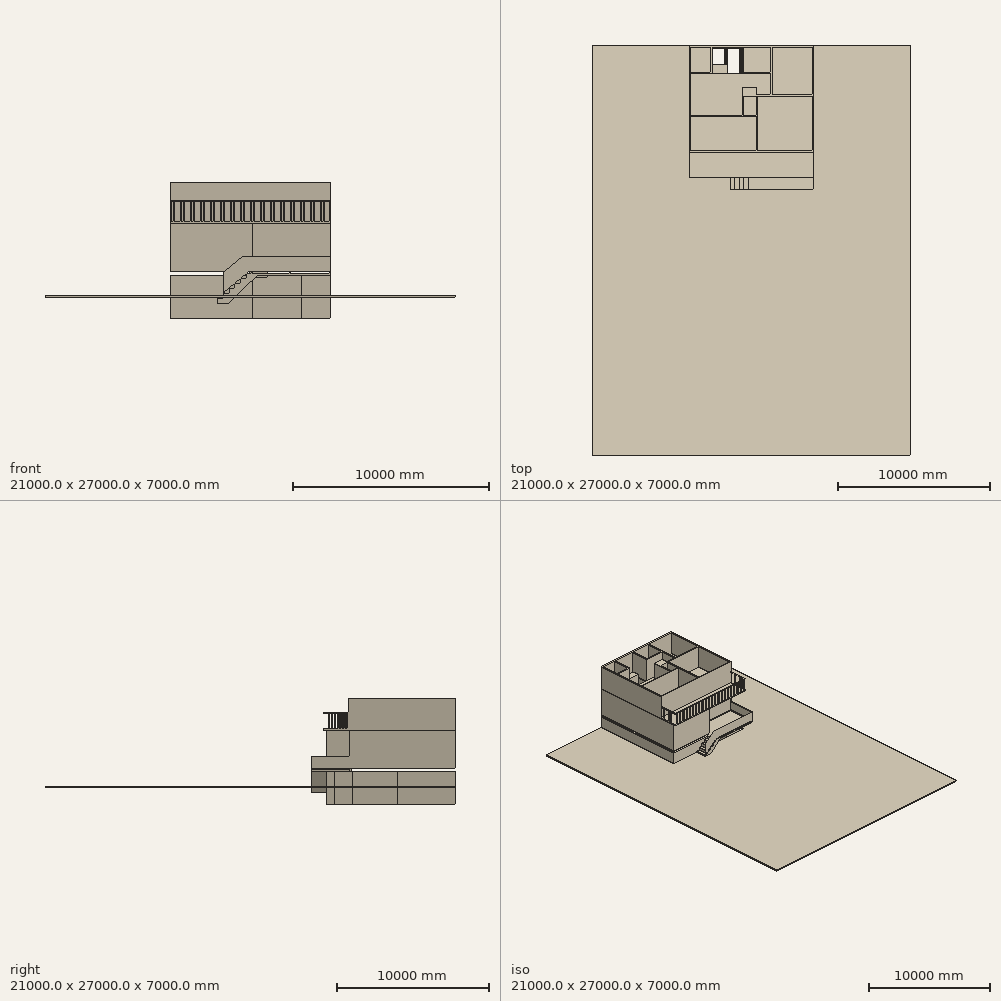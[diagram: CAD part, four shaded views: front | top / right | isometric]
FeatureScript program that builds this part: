
annotation { "Feature Type Name" : "Feature", "Feature Type Description" : "" }
export const myFeature = defineFeature(function(context is Context, id is Id, definition is map)
    precondition{}
    {
        {
            var Q0;
            Q0=qCreatedBy(makeId("Top.planeOp"),FACE);
            var sketch = newSketch(context, id + "F0", { "sketchPlane" : qUnion([Q0])});
            skLineSegment(sketch, "E0", {"start": v(-4100, -4250) * mm, "end": v(-4100, 4250) * mm});
            skLineSegment(sketch, "E1", {"start": v(-4100, 4250) * mm, "end": v(4100, 4250) * mm});
            skLineSegment(sketch, "E2", {"start": v(4100, 4250) * mm, "end": v(4100, -2750) * mm});
            skLineSegment(sketch, "E3", {"start": v(4100, -2750) * mm, "end": v(100, -2750) * mm});
            skLineSegment(sketch, "E4", {"start": v(100, -2750) * mm, "end": v(100, -4250) * mm});
            skLineSegment(sketch, "E5", {"start": v(100, -4250) * mm, "end": v(-4100, -4250) * mm});
            skLineSegment(sketch, "E6", {"start": v(-3950, -4100) * mm, "end": v(-3950, 4100) * mm});
            skLineSegment(sketch, "E7", {"start": v(-3950, 4100) * mm, "end": v(3900, 4100) * mm});
            skLineSegment(sketch, "E8", {"start": v(3900, 4100) * mm, "end": v(3900, -2600) * mm});
            skLineSegment(sketch, "E9", {"start": v(3900, -2600) * mm, "end": v(-50, -2600) * mm});
            skLineSegment(sketch, "E10", {"start": v(-50, -2600) * mm, "end": v(-50, -4100) * mm});
            skLineSegment(sketch, "E11", {"start": v(-50, -4100) * mm, "end": v(-3950, -4100) * mm});
            skLineSegment(sketch, "E12.bottom", {"start": v(-2750, 4100) * mm, "end": v(-2650, 4100) * mm});
            skLineSegment(sketch, "E12.top", {"start": v(-2750, 2100) * mm, "end": v(-2650, 2100) * mm});
            skLineSegment(sketch, "E12.left", {"start": v(-2750, 4100) * mm, "end": v(-2750, 2100) * mm});
            skLineSegment(sketch, "E12.right", {"start": v(-2650, 4100) * mm, "end": v(-2650, 2100) * mm});
            skLineSegment(sketch, "E13", {"start": v(-3950, 3300) * mm, "end": v(-2750, 3300) * mm});
            skLineSegment(sketch, "E14", {"start": v(-3950, 3200) * mm, "end": v(-2750, 3200) * mm});
            skLineSegment(sketch, "E15", {"start": v(-3950, 800) * mm, "end": v(-650, 800) * mm});
            skLineSegment(sketch, "E16", {"start": v(-650, 800) * mm, "end": v(-650, 2100) * mm});
            skLineSegment(sketch, "E17", {"start": v(-650, 2100) * mm, "end": v(-1650, 2100) * mm});
            skLineSegment(sketch, "E18", {"start": v(-1650, 2100) * mm, "end": v(-1650, 4100) * mm});
            skLineSegment(sketch, "E19", {"start": v(-1650, 4100) * mm, "end": v(-1550, 4100) * mm});
            skLineSegment(sketch, "E20", {"start": v(-1550, 4100) * mm, "end": v(-1550, 2200) * mm});
            skLineSegment(sketch, "E21", {"start": v(-1550, 2200) * mm, "end": v(-550, 2200) * mm});
            skLineSegment(sketch, "E22", {"start": v(-550, 2200) * mm, "end": v(-550, 700) * mm});
            skLineSegment(sketch, "E23", {"start": v(-550, 700) * mm, "end": v(-3950, 700) * mm});
            skLineSegment(sketch, "E24", {"start": v(-3950, 700) * mm, "end": v(-3950, 800) * mm});
            skLineSegment(sketch, "E25", {"start": v(-550, 2200) * mm, "end": v(-550, 4100) * mm});
            skLineSegment(sketch, "E26", {"start": v(-650, 4100) * mm, "end": v(-650, 2200) * mm});
            skLineSegment(sketch, "E27", {"start": v(-550, 700) * mm, "end": v(3900, 700) * mm});
            skLineSegment(sketch, "E28", {"start": v(3900, 800) * mm, "end": v(-550, 800) * mm});
            skLineSegment(sketch, "E29", {"start": v(-650, 700) * mm, "end": v(-650, 400) * mm});
            skLineSegment(sketch, "E30", {"start": v(-650, 400) * mm, "end": v(0, -200) * mm});
            skLineSegment(sketch, "E31", {"start": v(0, -200) * mm, "end": v(300, -200) * mm});
            skLineSegment(sketch, "E32", {"start": v(300, -200) * mm, "end": v(300, 0) * mm});
            skLineSegment(sketch, "E33", {"start": v(1800, 4100) * mm, "end": v(1800, 800) * mm});
            skLineSegment(sketch, "E34", {"start": v(1900, 4100) * mm, "end": v(1900, 800) * mm});
            skLineSegment(sketch, "E35", {"start": v(300, 0) * mm, "end": v(300, 1300) * mm});
            skLineSegment(sketch, "E36", {"start": v(300, 1300) * mm, "end": v(-550, 1300) * mm});
            skSolve(sketch);
        }
        {
            var Q0;
            Q0=makeQuery(id+"F0.imprint","IMPRINT",FACE,{"disambiguationData":[TD([[makeQuery(id+"F0.imprint","IMPRINT",EDGE,{"derivedFrom":sQuery(id+"F0.wireOp",EDGE,"E15")}),-1.0]])]});
            var Q1;
            {var subQ3=sQuery(id+"F0.wireOp",EDGE,"E36");Q1=makeQuery(id+"F0.imprint","IMPRINT",FACE,{"disambiguationData":[TD([[makeQuery(id+"F0.imprint","IMPRINT",EDGE,{"derivedFrom":subQ3}),1.0]])]});}
            var Q2;
            {var subQ1=sQuery(id+"F0.wireOp",EDGE,"E22");var subQ3=sQuery(id+"F0.wireOp",EDGE,"E28");var subQ4=makeQuery(id+"F0.imprint","INTERSECT",VERTEX,{"derivedFrom":[subQ1,subQ3]});Q2=makeQuery(id+"F0.imprint","IMPRINT",FACE,{"disambiguationData":[TD([[makeQuery(id+"F0.imprint","IMPRINT",EDGE,{"disambiguationData":[TD([[subQ4,1.0]])],"derivedFrom":subQ3}),1.0]])]});}
            var Q3;
            {var subQ0=sQuery(id+"F0.wireOp",EDGE,"E29");Q3=makeQuery(id+"F0.imprint","IMPRINT",FACE,{"disambiguationData":[TD([[makeQuery(id+"F0.imprint","IMPRINT",EDGE,{"derivedFrom":subQ0}),1.0]])]});}
            var Q4;
            {var subQ3=sQuery(id+"F0.wireOp",EDGE,"E8");var subQ6=sQuery(id+"F0.wireOp",EDGE,"E27");var subQ9=makeQuery(id+"F0.imprint","INTERSECT",VERTEX,{"derivedFrom":[subQ3,subQ6]});Q4=makeQuery(id+"F0.imprint","IMPRINT",FACE,{"disambiguationData":[TD([[makeQuery(id+"F0.imprint","IMPRINT",EDGE,{"disambiguationData":[TD([[subQ9,1.0]])],"derivedFrom":subQ3}),-1.0]])]});}
            var Q5;
            {var subQ0=sQuery(id+"F0.wireOp",EDGE,"E33");Q5=makeQuery(id+"F0.imprint","IMPRINT",FACE,{"disambiguationData":[TD([[makeQuery(id+"F0.imprint","IMPRINT",EDGE,{"derivedFrom":subQ0}),1.0]])]});}
            var Q6;
            Q6=makeQuery(id+"F0.imprint","IMPRINT",FACE,{"disambiguationData":[TD([[makeQuery(id+"F0.imprint","IMPRINT",EDGE,{"derivedFrom":sQuery(id+"F0.wireOp",EDGE,"E0")}),-1.0]])]});
            var Q7;
            {var subQ0=sQuery(id+"F0.wireOp",EDGE,"E13");Q7=makeQuery(id+"F0.imprint","IMPRINT",FACE,{"disambiguationData":[TD([[makeQuery(id+"F0.imprint","IMPRINT",EDGE,{"derivedFrom":subQ0}),-1.0]])]});}
            var Q8;
            {var subQ3=sQuery(id+"F0.wireOp",EDGE,"E12.bottom");Q8=makeQuery(id+"F0.imprint","IMPRINT",FACE,{"disambiguationData":[TD([[makeQuery(id+"F0.imprint","IMPRINT",EDGE,{"derivedFrom":subQ3}),-1.0]])]});}
            var Q9;
            {var subQ0=sQuery(id+"F0.wireOp",EDGE,"E25");Q9=makeQuery(id+"F0.imprint","IMPRINT",FACE,{"disambiguationData":[TD([[makeQuery(id+"F0.imprint","IMPRINT",EDGE,{"derivedFrom":subQ0}),1.0]])]});}
            extrude(context, id + "F1", {"entities" : qUnion([Q0, Q1, Q2, Q3, Q4, Q5, Q6, Q7, Q8, Q9]), "depth" : 2500 * mm, "offsetDistance" : 25 * mm});
        }
        {
            var Q0;
            Q0=makeQuery(id+"F1.opExtrude","CAP_FACE",FACE,{"disambiguationData":[OSD([sQuery(id+"F0.wireOp",EDGE,"E0"),sQuery(id+"F0.wireOp",EDGE,"E1"),sQuery(id+"F0.wireOp",EDGE,"E2"),sQuery(id+"F0.wireOp",EDGE,"E3"),sQuery(id+"F0.wireOp",EDGE,"E4"),sQuery(id+"F0.wireOp",EDGE,"E5"),sQuery(id+"F0.wireOp",EDGE,"E6"),sQuery(id+"F0.wireOp",EDGE,"E7"),sQuery(id+"F0.wireOp",EDGE,"E8"),sQuery(id+"F0.wireOp",EDGE,"E9"),sQuery(id+"F0.wireOp",EDGE,"E10"),sQuery(id+"F0.wireOp",EDGE,"E11"),sQuery(id+"F0.wireOp",EDGE,"E12.top"),sQuery(id+"F0.wireOp",EDGE,"E12.left"),sQuery(id+"F0.wireOp",EDGE,"E12.right"),sQuery(id+"F0.wireOp",EDGE,"E13"),sQuery(id+"F0.wireOp",EDGE,"E14"),sQuery(id+"F0.wireOp",EDGE,"E15"),sQuery(id+"F0.wireOp",EDGE,"E16"),sQuery(id+"F0.wireOp",EDGE,"E17"),sQuery(id+"F0.wireOp",EDGE,"E18"),sQuery(id+"F0.wireOp",EDGE,"E20"),sQuery(id+"F0.wireOp",EDGE,"E21"),sQuery(id+"F0.wireOp",EDGE,"E22"),sQuery(id+"F0.wireOp",EDGE,"E23"),sQuery(id+"F0.wireOp",EDGE,"E25"),sQuery(id+"F0.wireOp",EDGE,"E26"),sQuery(id+"F0.wireOp",EDGE,"E27"),sQuery(id+"F0.wireOp",EDGE,"E28"),sQuery(id+"F0.wireOp",EDGE,"E29"),sQuery(id+"F0.wireOp",EDGE,"E30"),sQuery(id+"F0.wireOp",EDGE,"E31"),sQuery(id+"F0.wireOp",EDGE,"E32")])],"isStart":true});
            cPlane(context, id + "F2", {"entities" : qUnion([Q0]), "cplaneType" : CPlaneType.OFFSET, "offset" : 200 * mm, "width" : 150 * mm, "height" : 150 * mm});
        }
        {
            var Q0;
            Q0=makeQuery(id+"F1.opExtrude","SWEPT_FACE",FACE,{"disambiguationData":[OSD([sQuery(id+"F0.wireOp",EDGE,"E9")])]});
            var sketch = newSketch(context, id + "F3", { "sketchPlane" : qUnion([Q0])});
            skLineSegment(sketch, "E37.bottom", {"start": v(50, 1) * mm, "end": v(-850, 1) * mm});
            skLineSegment(sketch, "E37.top", {"start": v(50, -299) * mm, "end": v(-850, -299) * mm});
            skLineSegment(sketch, "E37.left", {"start": v(50, 1) * mm, "end": v(50, -299) * mm});
            skLineSegment(sketch, "E37.right", {"start": v(-850, 1) * mm, "end": v(-850, -299) * mm});
            skSolve(sketch);
        }
        {
            var Q0;
            Q0=qCreatedBy(id+"F2.planeOp",FACE);
            var sketch = newSketch(context, id + "F4", { "sketchPlane" : qUnion([Q0])});
            skLineSegment(sketch, "E38.bottom", {"start": v(100, 2750) * mm, "end": v(4100, 2750) * mm});
            skLineSegment(sketch, "E38.top", {"start": v(100, 5250) * mm, "end": v(4100, 5250) * mm});
            skLineSegment(sketch, "E38.left", {"start": v(100, 2750) * mm, "end": v(100, 5250) * mm});
            skLineSegment(sketch, "E38.right", {"start": v(4100, 2750) * mm, "end": v(4100, 5250) * mm});
            skSolve(sketch);
        }
        {
            var Q0;
            {var subQ0=sQuery(id+"F3.wireOp",EDGE,"E37.top");Q0=makeQuery(id+"F3.imprint","IMPRINT",FACE,{"disambiguationData":[TD([[makeQuery(id+"F3.imprint","IMPRINT",EDGE,{"derivedFrom":subQ0}),-1.0]])]});}
            extrude(context, id + "F5", {"entities" : qUnion([Q0]), "operationType" : NewBodyOperationType.ADD, "oppositeDirection" : true, "depth" : 400 * mm, "offsetDistance" : 25 * mm});
        }
        {
            var Q0;
            Q0=makeQuery(id+"F4.imprint","IMPRINT",FACE,{"disambiguationData":[TD([[makeQuery(id+"F4.imprint","IMPRINT",EDGE,{"derivedFrom":sQuery(id+"F4.wireOp",EDGE,"E38.bottom")}),1.0]])]});
            extrude(context, id + "F6", {"entities" : qUnion([Q0]), "operationType" : NewBodyOperationType.ADD, "oppositeDirection" : true, "depth" : 100 * mm, "offsetDistance" : 25 * mm});
        }
        {
            var Q0;
            Q0=makeQuery(id+"F6.opExtrude","SWEPT_FACE",FACE,{"disambiguationData":[OSD([sQuery(id+"F4.wireOp",EDGE,"E38.top")])]});
            var sketch = newSketch(context, id + "F7", { "sketchPlane" : qUnion([Q0])});
            skLineSegment(sketch, "E39", {"start": v(100, -100) * mm, "end": v(-200, -100) * mm});
            skLineSegment(sketch, "E40", {"start": v(-200, -100) * mm, "end": v(-200, -350) * mm});
            skLineSegment(sketch, "E41", {"start": v(-200, -350) * mm, "end": v(-500, -350) * mm});
            skLineSegment(sketch, "E42", {"start": v(-500, -350) * mm, "end": v(-500, -600) * mm});
            skLineSegment(sketch, "E43", {"start": v(-500, -600) * mm, "end": v(-800, -600) * mm});
            skLineSegment(sketch, "E44", {"start": v(-800, -600) * mm, "end": v(-800, -850) * mm});
            skLineSegment(sketch, "E45", {"start": v(-800, -850) * mm, "end": v(-1100, -850) * mm});
            skLineSegment(sketch, "E46", {"start": v(-1100, -850) * mm, "end": v(-1100, -1100) * mm});
            skLineSegment(sketch, "E47", {"start": v(-1100, -1100) * mm, "end": v(-1400, -1100) * mm});
            skLineSegment(sketch, "E48", {"start": v(-1400, -1100) * mm, "end": v(-1400, -1350) * mm});
            skLineSegment(sketch, "E49", {"start": v(-1400, -1350) * mm, "end": v(-1700, -1350) * mm});
            skLineSegment(sketch, "E50", {"start": v(-1700, -1350) * mm, "end": v(-1700, -1600) * mm});
            skLineSegment(sketch, "E51", {"start": v(-1700, -1600) * mm, "end": v(-1108.65, -1600) * mm});
            skLineSegment(sketch, "E52", {"start": v(-1108.65, -1600) * mm, "end": v(350, -200) * mm});
            skLineSegment(sketch, "E53", {"start": v(350, -200) * mm, "end": v(100, -100) * mm});
            skSolve(sketch);
        }
        {
            var Q0;
            Q0=makeQuery(id+"F7.imprint","IMPRINT",FACE,{"disambiguationData":[TD([[makeQuery(id+"F7.imprint","IMPRINT",EDGE,{"derivedFrom":sQuery(id+"F7.wireOp",EDGE,"E39")}),1.0]])]});
            var Q1;
            Q1=makeQuery(id+"F1.opExtrude","SWEPT_FACE",FACE,{"disambiguationData":[OSD([sQuery(id+"F0.wireOp",EDGE,"E5")])]});
            extrude(context, id + "F8", {"entities" : qUnion([Q0]), "operationType" : NewBodyOperationType.ADD, "endBound" : BoundingType.UP_TO_SURFACE, "oppositeDirection" : true, "depth" : 25 * mm, "endBoundEntityFace" : qUnion([Q1]), "offsetDistance" : 25 * mm});
        }
        {
            var Q0;
            {var subQ0=sQuery(id+"F4.wireOp",EDGE,"E38.top");Q0=makeQuery(id+"F8.boolean.opBoolean","MERGE",FACE,{"derivedFrom":[makeQuery(id+"F6.opExtrude","SWEPT_FACE",FACE,{"disambiguationData":[OSD([subQ0])]}),makeQuery(id+"F8.opExtrude","CAP_FACE",FACE,{"disambiguationData":[OSD([subQ0,sQuery(id+"F4.wireOp",EDGE,"E38.left"),sQuery(id+"F7.wireOp",EDGE,"E39"),sQuery(id+"F7.wireOp",EDGE,"E40"),sQuery(id+"F7.wireOp",EDGE,"E41"),sQuery(id+"F7.wireOp",EDGE,"E42"),sQuery(id+"F7.wireOp",EDGE,"E43"),sQuery(id+"F7.wireOp",EDGE,"E44"),sQuery(id+"F7.wireOp",EDGE,"E45"),sQuery(id+"F7.wireOp",EDGE,"E46"),sQuery(id+"F7.wireOp",EDGE,"E47"),sQuery(id+"F7.wireOp",EDGE,"E48"),sQuery(id+"F7.wireOp",EDGE,"E49"),sQuery(id+"F7.wireOp",EDGE,"E50"),sQuery(id+"F7.wireOp",EDGE,"E51"),sQuery(id+"F7.wireOp",EDGE,"E52")])],"isStart":true})]});}
            var sketch = newSketch(context, id + "F9", { "sketchPlane" : qUnion([Q0])});
            skLineSegment(sketch, "E54", {"start": v(-1400, -1100) * mm, "end": v(-1400, -45.62) * mm});
            skLineSegment(sketch, "E55", {"start": v(-1400, -45.62) * mm, "end": v(-385.26, 800) * mm});
            skLineSegment(sketch, "E56", {"start": v(-385.26, 800) * mm, "end": v(4100, 800) * mm});
            skLineSegment(sketch, "E57", {"start": v(4100, 800) * mm, "end": v(4100, -100) * mm});
            skLineSegment(sketch, "E58", {"start": v(4100, -100) * mm, "end": v(4050, -100) * mm});
            skLineSegment(sketch, "E59", {"start": v(4050, -100) * mm, "end": v(4050, 0) * mm});
            skLineSegment(sketch, "E60", {"start": v(4050, 0) * mm, "end": v(2070.72, 0) * mm});
            skLineSegment(sketch, "E61", {"start": v(2070.72, 0) * mm, "end": v(2070.72, -100) * mm});
            skLineSegment(sketch, "E62", {"start": v(2070.72, -100) * mm, "end": v(2020.72, -100) * mm});
            skLineSegment(sketch, "E63", {"start": v(2020.72, -100) * mm, "end": v(2020.72, 0) * mm});
            skLineSegment(sketch, "E64", {"start": v(2020.72, 0) * mm, "end": v(100, 0) * mm});
            skLineSegment(sketch, "E65", {"start": v(100, 0) * mm, "end": v(100, -100) * mm});
            skLineSegment(sketch, "E66", {"start": v(100, -100) * mm, "end": v(50, -100) * mm});
            skLineSegment(sketch, "E67", {"start": v(50, -100) * mm, "end": v(50, 0) * mm});
            skLineSegment(sketch, "E68", {"start": v(50, 0) * mm, "end": v(-95.62, 0) * mm});
            skLineSegment(sketch, "E69", {"start": v(-95.62, 0) * mm, "end": v(-1350, -1045.32) * mm});
            skLineSegment(sketch, "E70", {"start": v(-1350, -1045.32) * mm, "end": v(-1350, -1100) * mm});
            skLineSegment(sketch, "E71", {"start": v(-1350, -1100) * mm, "end": v(-1400, -1100) * mm});
            skSolve(sketch);
        }
        {
            var Q0;
            Q0=makeQuery(id+"F9.imprint","IMPRINT",FACE,{"disambiguationData":[TD([[makeQuery(id+"F9.imprint","IMPRINT",EDGE,{"derivedFrom":sQuery(id+"F9.wireOp",EDGE,"E54")}),-1.0]])]});
            extrude(context, id + "F10", {"entities" : qUnion([Q0]), "operationType" : NewBodyOperationType.ADD, "oppositeDirection" : true, "depth" : 10 * mm, "offsetDistance" : 25 * mm});
        }
        {
            var Q0;
            Q0=makeQuery(id+"F10.boolean.opBoolean","MERGE",FACE,{"derivedFrom":[makeQuery(id+"F6.opExtrude","SWEPT_FACE",FACE,{"disambiguationData":[OSD([sQuery(id+"F4.wireOp",EDGE,"E38.right")])]}),makeQuery(id+"F10.opExtrude","SWEPT_FACE",FACE,{"disambiguationData":[OSD([sQuery(id+"F9.wireOp",EDGE,"E57")])]})]});
            var sketch = newSketch(context, id + "F11", { "sketchPlane" : qUnion([Q0])});
            skLineSegment(sketch, "E72.bottom", {"start": v(-5250, 800) * mm, "end": v(-2750, 800) * mm});
            skLineSegment(sketch, "E72.top", {"start": v(-5250, 0) * mm, "end": v(-2750, 0) * mm});
            skLineSegment(sketch, "E72.left", {"start": v(-5250, 800) * mm, "end": v(-5250, 0) * mm});
            skLineSegment(sketch, "E72.right", {"start": v(-2750, 800) * mm, "end": v(-2750, 0) * mm});
            skSolve(sketch);
        }
        {
            var Q0;
            {var subQ3=sQuery(id+"F11.wireOp",EDGE,"E72.right");Q0=makeQuery(id+"F11.imprint","IMPRINT",FACE,{"disambiguationData":[TD([[makeQuery(id+"F11.imprint","IMPRINT",EDGE,{"derivedFrom":subQ3}),-1.0]])]});}
            extrude(context, id + "F12", {"entities" : qUnion([Q0]), "operationType" : NewBodyOperationType.ADD, "oppositeDirection" : true, "depth" : 10 * mm, "offsetDistance" : 25 * mm});
        }
        {
            var Q0;
            Q0=makeQuery(id+"F1.opExtrude","CAP_FACE",FACE,{"disambiguationData":[OSD([sQuery(id+"F0.wireOp",EDGE,"E0"),sQuery(id+"F0.wireOp",EDGE,"E1"),sQuery(id+"F0.wireOp",EDGE,"E2"),sQuery(id+"F0.wireOp",EDGE,"E3"),sQuery(id+"F0.wireOp",EDGE,"E4"),sQuery(id+"F0.wireOp",EDGE,"E5"),sQuery(id+"F0.wireOp",EDGE,"E6"),sQuery(id+"F0.wireOp",EDGE,"E7"),sQuery(id+"F0.wireOp",EDGE,"E8"),sQuery(id+"F0.wireOp",EDGE,"E9"),sQuery(id+"F0.wireOp",EDGE,"E10"),sQuery(id+"F0.wireOp",EDGE,"E11"),sQuery(id+"F0.wireOp",EDGE,"E12.top"),sQuery(id+"F0.wireOp",EDGE,"E12.left"),sQuery(id+"F0.wireOp",EDGE,"E12.right"),sQuery(id+"F0.wireOp",EDGE,"E13"),sQuery(id+"F0.wireOp",EDGE,"E14"),sQuery(id+"F0.wireOp",EDGE,"E15"),sQuery(id+"F0.wireOp",EDGE,"E16"),sQuery(id+"F0.wireOp",EDGE,"E17"),sQuery(id+"F0.wireOp",EDGE,"E18"),sQuery(id+"F0.wireOp",EDGE,"E20"),sQuery(id+"F0.wireOp",EDGE,"E21"),sQuery(id+"F0.wireOp",EDGE,"E22"),sQuery(id+"F0.wireOp",EDGE,"E23"),sQuery(id+"F0.wireOp",EDGE,"E25"),sQuery(id+"F0.wireOp",EDGE,"E26"),sQuery(id+"F0.wireOp",EDGE,"E27"),sQuery(id+"F0.wireOp",EDGE,"E28"),sQuery(id+"F0.wireOp",EDGE,"E29"),sQuery(id+"F0.wireOp",EDGE,"E30"),sQuery(id+"F0.wireOp",EDGE,"E31"),sQuery(id+"F0.wireOp",EDGE,"E32")])],"isStart":false});
            cPlane(context, id + "F13", {"entities" : qUnion([Q0]), "cplaneType" : CPlaneType.OFFSET, "offset" : 0 * mm, "width" : 150 * mm, "height" : 150 * mm});
        }
        {
            var Q0;
            Q0=qCreatedBy(id+"F13.planeOp",FACE);
            var sketch = newSketch(context, id + "F14", { "sketchPlane" : qUnion([Q0])});
            skLineSegment(sketch, "E73.bottom", {"start": v(-4100, 4250) * mm, "end": v(4100, 4250) * mm});
            skLineSegment(sketch, "E73.top", {"start": v(-4100, -4450) * mm, "end": v(4100, -4450) * mm});
            skLineSegment(sketch, "E73.left", {"start": v(-4100, 4250) * mm, "end": v(-4100, -4450) * mm});
            skLineSegment(sketch, "E73.right", {"start": v(4100, 4250) * mm, "end": v(4100, -4450) * mm});
            skLineSegment(sketch, "E74.bottom", {"start": v(-2600, 4100) * mm, "end": v(-600, 4100) * mm});
            skLineSegment(sketch, "E74.top", {"start": v(-2600, 2400) * mm, "end": v(-600, 2400) * mm});
            skLineSegment(sketch, "E74.left", {"start": v(-2600, 4100) * mm, "end": v(-2600, 2400) * mm});
            skLineSegment(sketch, "E74.right", {"start": v(-600, 4100) * mm, "end": v(-600, 2400) * mm});
            skSolve(sketch);
        }
        {
            var Q0;
            Q0=makeQuery(id+"F14.imprint","IMPRINT",FACE,{"disambiguationData":[TD([[makeQuery(id+"F14.imprint","IMPRINT",EDGE,{"derivedFrom":sQuery(id+"F14.wireOp",EDGE,"E73.bottom")}),-1.0]])]});
            extrude(context, id + "F15", {"entities" : qUnion([Q0]), "depth" : 100 * mm, "offsetDistance" : 25 * mm});
        }
        {
            var Q0;
            Q0=makeQuery(id+"F15.opExtrude","CAP_FACE",FACE,{"disambiguationData":[OSD([sQuery(id+"F14.wireOp",EDGE,"E73.bottom"),sQuery(id+"F14.wireOp",EDGE,"E73.top"),sQuery(id+"F14.wireOp",EDGE,"E73.left"),sQuery(id+"F14.wireOp",EDGE,"E73.right")])],"isStart":false});
            var sketch = newSketch(context, id + "F16", { "sketchPlane" : qUnion([Q0])});
            skLineSegment(sketch, "E75", {"start": v(-4100, -2780) * mm, "end": v(4100, -2780) * mm});
            skLineSegment(sketch, "E76", {"start": v(-2600, 4100) * mm, "end": v(-4000, 4100) * mm});
            skLineSegment(sketch, "E77", {"start": v(-4000, 4100) * mm, "end": v(-4000, -2680) * mm});
            skLineSegment(sketch, "E78", {"start": v(-4000, -2680) * mm, "end": v(4000, -2680) * mm});
            skLineSegment(sketch, "E79", {"start": v(4000, -2680) * mm, "end": v(4000, 4100) * mm});
            skLineSegment(sketch, "E80", {"start": v(4000, 4100) * mm, "end": v(-2600, 4100) * mm});
            skLineSegment(sketch, "E81", {"start": v(-2700, 4100) * mm, "end": v(-2700, 2500) * mm});
            skLineSegment(sketch, "E82", {"start": v(-2700, 2500) * mm, "end": v(-4000, 2500) * mm});
            skLineSegment(sketch, "E83", {"start": v(-4000, 2500) * mm, "end": v(-4000, 2400) * mm});
            skLineSegment(sketch, "E84", {"start": v(-4000, 2400) * mm, "end": v(-2600, 2400) * mm});
            skLineSegment(sketch, "E85", {"start": v(-2600, 2400) * mm, "end": v(-2600, 4100) * mm});
            skLineSegment(sketch, "E86", {"start": v(-2600, 4100) * mm, "end": v(-2700, 4100) * mm});
            skLineSegment(sketch, "E87", {"start": v(-600, 4100) * mm, "end": v(-600, 2400) * mm});
            skLineSegment(sketch, "E88", {"start": v(-600, 2400) * mm, "end": v(1350, 2400) * mm});
            skLineSegment(sketch, "E89", {"start": v(1350, 2400) * mm, "end": v(1350, 4100) * mm});
            skLineSegment(sketch, "E90", {"start": v(1350, 4100) * mm, "end": v(-600, 4100) * mm});
            skLineSegment(sketch, "E91", {"start": v(-500, 4100) * mm, "end": v(-500, 2500) * mm});
            skLineSegment(sketch, "E92", {"start": v(-500, 2500) * mm, "end": v(1250, 2500) * mm});
            skLineSegment(sketch, "E93", {"start": v(1250, 2500) * mm, "end": v(1250, 4100) * mm});
            skLineSegment(sketch, "E94", {"start": v(1350, 2400) * mm, "end": v(1350, 1000) * mm});
            skLineSegment(sketch, "E95", {"start": v(1350, 1000) * mm, "end": v(4000, 1000) * mm});
            skLineSegment(sketch, "E96", {"start": v(4000, 1000) * mm, "end": v(4000, 900) * mm});
            skLineSegment(sketch, "E97", {"start": v(4000, 900) * mm, "end": v(1250, 900) * mm});
            skLineSegment(sketch, "E98", {"start": v(1250, 900) * mm, "end": v(1250, 2400) * mm});
            skLineSegment(sketch, "E99", {"start": v(1250, 2400) * mm, "end": v(1350, 2400) * mm});
            skLineSegment(sketch, "E100", {"start": v(1250, 900) * mm, "end": v(-500, 900) * mm});
            skLineSegment(sketch, "E101", {"start": v(-500, 900) * mm, "end": v(-500, -340) * mm});
            skPoint(sketch, "E101.endSnap0", {"position": v(0, -2680) * mm});
            skLineSegment(sketch, "E102", {"start": v(-500, -2680) * mm, "end": v(-600, -2680) * mm});
            skLineSegment(sketch, "E103", {"start": v(-600, -340) * mm, "end": v(-600, 1000) * mm});
            skLineSegment(sketch, "E104", {"start": v(-600, 1000) * mm, "end": v(1250, 1000) * mm});
            skLineSegment(sketch, "E105", {"start": v(1250, 1000) * mm, "end": v(1250, 900) * mm});
            skLineSegment(sketch, "E106", {"start": v(-4000, -340) * mm, "end": v(-600, -340) * mm});
            skLineSegment(sketch, "E107", {"start": v(300, -440) * mm, "end": v(-4000, -440) * mm});
            skLineSegment(sketch, "E108", {"start": v(-4000, -440) * mm, "end": v(-4000, -340) * mm});
            skLineSegment(sketch, "E109", {"start": v(-2600, 2400) * mm, "end": v(-1600, 2400) * mm});
            skLineSegment(sketch, "E110", {"start": v(-4100, -2780) * mm, "end": v(-4100, 4250) * mm});
            skLineSegment(sketch, "E111", {"start": v(-4100, 4250) * mm, "end": v(4100, 4250) * mm});
            skLineSegment(sketch, "E112", {"start": v(4100, 4250) * mm, "end": v(4100, -2780) * mm});
            skLineSegment(sketch, "E113", {"start": v(-1600, 2400) * mm, "end": v(-1600, 3000) * mm});
            skLineSegment(sketch, "E114", {"start": v(-1600, 3000) * mm, "end": v(-2600, 3000) * mm});
            skLineSegment(sketch, "E115", {"start": v(-600, 1000) * mm, "end": v(-600, 1500) * mm});
            skLineSegment(sketch, "E116", {"start": v(-600, 1500) * mm, "end": v(350, 1500) * mm});
            skLineSegment(sketch, "E117", {"start": v(350, 1500) * mm, "end": v(350, 1000) * mm});
            skPoint(sketch, "E118.endSnap0", {"position": v(375, 900) * mm});
            skLineSegment(sketch, "E119", {"start": v(300, -2680) * mm, "end": v(300, 900) * mm});
            skLineSegment(sketch, "E120", {"start": v(400, 900) * mm, "end": v(400, -2680) * mm});
            skLineSegment(sketch, "E121", {"start": v(-500, -340) * mm, "end": v(300, -340) * mm});
            skLineSegment(sketch, "E122.bottom", {"start": v(-4100, -2880) * mm, "end": v(-4070, -2880) * mm});
            skLineSegment(sketch, "E122.top", {"start": v(-4100, -2910) * mm, "end": v(-4070, -2910) * mm});
            skLineSegment(sketch, "E122.left", {"start": v(-4100, -2880) * mm, "end": v(-4100, -2910) * mm});
            skLineSegment(sketch, "E122.right", {"start": v(-4070, -2880) * mm, "end": v(-4070, -2910) * mm});
            skLineSegment(sketch, "E123.0.1.0", {"start": v(-4100, -3080) * mm, "end": v(-4100, -3110) * mm});
            skLineSegment(sketch, "E123.0.1.1", {"start": v(-4100, -3080) * mm, "end": v(-4070, -3080) * mm});
            skLineSegment(sketch, "E123.0.1.2", {"start": v(-4070, -3080) * mm, "end": v(-4070, -3110) * mm});
            skLineSegment(sketch, "E123.0.1.3", {"start": v(-4100, -3110) * mm, "end": v(-4070, -3110) * mm});
            skLineSegment(sketch, "E123.0.2.0", {"start": v(-4100, -3280) * mm, "end": v(-4100, -3310) * mm});
            skLineSegment(sketch, "E123.0.2.1", {"start": v(-4100, -3280) * mm, "end": v(-4070, -3280) * mm});
            skLineSegment(sketch, "E123.0.2.2", {"start": v(-4070, -3280) * mm, "end": v(-4070, -3310) * mm});
            skLineSegment(sketch, "E123.0.2.3", {"start": v(-4100, -3310) * mm, "end": v(-4070, -3310) * mm});
            skLineSegment(sketch, "E123.0.3.0", {"start": v(-4100, -3480) * mm, "end": v(-4100, -3510) * mm});
            skLineSegment(sketch, "E123.0.3.1", {"start": v(-4100, -3480) * mm, "end": v(-4070, -3480) * mm});
            skLineSegment(sketch, "E123.0.3.2", {"start": v(-4070, -3480) * mm, "end": v(-4070, -3510) * mm});
            skLineSegment(sketch, "E123.0.3.3", {"start": v(-4100, -3510) * mm, "end": v(-4070, -3510) * mm});
            skLineSegment(sketch, "E123.0.4.0", {"start": v(-4100, -3680) * mm, "end": v(-4100, -3710) * mm});
            skLineSegment(sketch, "E123.0.4.1", {"start": v(-4100, -3680) * mm, "end": v(-4070, -3680) * mm});
            skLineSegment(sketch, "E123.0.4.2", {"start": v(-4070, -3680) * mm, "end": v(-4070, -3710) * mm});
            skLineSegment(sketch, "E123.0.4.3", {"start": v(-4100, -3710) * mm, "end": v(-4070, -3710) * mm});
            skLineSegment(sketch, "E123.0.5.0", {"start": v(-4100, -3880) * mm, "end": v(-4100, -3910) * mm});
            skLineSegment(sketch, "E123.0.5.1", {"start": v(-4100, -3880) * mm, "end": v(-4070, -3880) * mm});
            skLineSegment(sketch, "E123.0.5.2", {"start": v(-4070, -3880) * mm, "end": v(-4070, -3910) * mm});
            skLineSegment(sketch, "E123.0.5.3", {"start": v(-4100, -3910) * mm, "end": v(-4070, -3910) * mm});
            skLineSegment(sketch, "E123.0.6.0", {"start": v(-4100, -4080) * mm, "end": v(-4100, -4110) * mm});
            skLineSegment(sketch, "E123.0.6.1", {"start": v(-4100, -4080) * mm, "end": v(-4070, -4080) * mm});
            skLineSegment(sketch, "E123.0.6.2", {"start": v(-4070, -4080) * mm, "end": v(-4070, -4110) * mm});
            skLineSegment(sketch, "E123.0.6.3", {"start": v(-4100, -4110) * mm, "end": v(-4070, -4110) * mm});
            skLineSegment(sketch, "E123.0.7.0", {"start": v(-4100, -4280) * mm, "end": v(-4100, -4310) * mm});
            skLineSegment(sketch, "E123.0.7.1", {"start": v(-4100, -4280) * mm, "end": v(-4070, -4280) * mm});
            skLineSegment(sketch, "E123.0.7.2", {"start": v(-4070, -4280) * mm, "end": v(-4070, -4310) * mm});
            skLineSegment(sketch, "E123.0.7.3", {"start": v(-4100, -4310) * mm, "end": v(-4070, -4310) * mm});
            skLineSegment(sketch, "E123.direction1", {"start": v(-4100, -2910) * mm, "end": v(-4075, -2910) * mm, "construction": true});
            skLineSegment(sketch, "E123.direction2", {"start": v(-4100, -2910) * mm, "end": v(-4100, -3110) * mm, "construction": true});
            skLineSegment(sketch, "E124.bottom", {"start": v(-4100, -4450) * mm, "end": v(-4070, -4450) * mm});
            skLineSegment(sketch, "E124.top", {"start": v(-4100, -4420) * mm, "end": v(-4070, -4420) * mm});
            skLineSegment(sketch, "E124.left", {"start": v(-4100, -4450) * mm, "end": v(-4100, -4420) * mm});
            skLineSegment(sketch, "E124.right", {"start": v(-4070, -4450) * mm, "end": v(-4070, -4420) * mm});
            skLineSegment(sketch, "E125.1.0.0", {"start": v(-3929.17, -4420) * mm, "end": v(-3899.17, -4420) * mm});
            skLineSegment(sketch, "E125.1.0.1", {"start": v(-3899.17, -4450) * mm, "end": v(-3899.17, -4420) * mm});
            skLineSegment(sketch, "E125.1.0.2", {"start": v(-3929.17, -4450) * mm, "end": v(-3899.17, -4450) * mm});
            skLineSegment(sketch, "E125.1.0.3", {"start": v(-3929.17, -4450) * mm, "end": v(-3929.17, -4420) * mm});
            skLineSegment(sketch, "E125.2.0.0", {"start": v(-3758.33, -4420) * mm, "end": v(-3728.33, -4420) * mm});
            skLineSegment(sketch, "E125.2.0.1", {"start": v(-3728.33, -4450) * mm, "end": v(-3728.33, -4420) * mm});
            skLineSegment(sketch, "E125.2.0.2", {"start": v(-3758.33, -4450) * mm, "end": v(-3728.33, -4450) * mm});
            skLineSegment(sketch, "E125.2.0.3", {"start": v(-3758.33, -4450) * mm, "end": v(-3758.33, -4420) * mm});
            skLineSegment(sketch, "E125.3.0.0", {"start": v(-3587.5, -4420) * mm, "end": v(-3557.5, -4420) * mm});
            skLineSegment(sketch, "E125.3.0.1", {"start": v(-3557.5, -4450) * mm, "end": v(-3557.5, -4420) * mm});
            skLineSegment(sketch, "E125.3.0.2", {"start": v(-3587.5, -4450) * mm, "end": v(-3557.5, -4450) * mm});
            skLineSegment(sketch, "E125.3.0.3", {"start": v(-3587.5, -4450) * mm, "end": v(-3587.5, -4420) * mm});
            skLineSegment(sketch, "E125.4.0.0", {"start": v(-3416.67, -4420) * mm, "end": v(-3386.67, -4420) * mm});
            skLineSegment(sketch, "E125.4.0.1", {"start": v(-3386.67, -4450) * mm, "end": v(-3386.67, -4420) * mm});
            skLineSegment(sketch, "E125.4.0.2", {"start": v(-3416.67, -4450) * mm, "end": v(-3386.67, -4450) * mm});
            skLineSegment(sketch, "E125.4.0.3", {"start": v(-3416.67, -4450) * mm, "end": v(-3416.67, -4420) * mm});
            skLineSegment(sketch, "E125.5.0.0", {"start": v(-3245.83, -4420) * mm, "end": v(-3215.83, -4420) * mm});
            skLineSegment(sketch, "E125.5.0.1", {"start": v(-3215.83, -4450) * mm, "end": v(-3215.83, -4420) * mm});
            skLineSegment(sketch, "E125.5.0.2", {"start": v(-3245.83, -4450) * mm, "end": v(-3215.83, -4450) * mm});
            skLineSegment(sketch, "E125.5.0.3", {"start": v(-3245.83, -4450) * mm, "end": v(-3245.83, -4420) * mm});
            skLineSegment(sketch, "E125.6.0.0", {"start": v(-3075, -4420) * mm, "end": v(-3045, -4420) * mm});
            skLineSegment(sketch, "E125.6.0.1", {"start": v(-3045, -4450) * mm, "end": v(-3045, -4420) * mm});
            skLineSegment(sketch, "E125.6.0.2", {"start": v(-3075, -4450) * mm, "end": v(-3045, -4450) * mm});
            skLineSegment(sketch, "E125.6.0.3", {"start": v(-3075, -4450) * mm, "end": v(-3075, -4420) * mm});
            skLineSegment(sketch, "E125.7.0.0", {"start": v(-2904.17, -4420) * mm, "end": v(-2874.17, -4420) * mm});
            skLineSegment(sketch, "E125.7.0.1", {"start": v(-2874.17, -4450) * mm, "end": v(-2874.17, -4420) * mm});
            skLineSegment(sketch, "E125.7.0.2", {"start": v(-2904.17, -4450) * mm, "end": v(-2874.17, -4450) * mm});
            skLineSegment(sketch, "E125.7.0.3", {"start": v(-2904.17, -4450) * mm, "end": v(-2904.17, -4420) * mm});
            skLineSegment(sketch, "E125.8.0.0", {"start": v(-2733.33, -4420) * mm, "end": v(-2703.33, -4420) * mm});
            skLineSegment(sketch, "E125.8.0.1", {"start": v(-2703.33, -4450) * mm, "end": v(-2703.33, -4420) * mm});
            skLineSegment(sketch, "E125.8.0.2", {"start": v(-2733.33, -4450) * mm, "end": v(-2703.33, -4450) * mm});
            skLineSegment(sketch, "E125.8.0.3", {"start": v(-2733.33, -4450) * mm, "end": v(-2733.33, -4420) * mm});
            skLineSegment(sketch, "E125.9.0.0", {"start": v(-2562.5, -4420) * mm, "end": v(-2532.5, -4420) * mm});
            skLineSegment(sketch, "E125.9.0.1", {"start": v(-2532.5, -4450) * mm, "end": v(-2532.5, -4420) * mm});
            skLineSegment(sketch, "E125.9.0.2", {"start": v(-2562.5, -4450) * mm, "end": v(-2532.5, -4450) * mm});
            skLineSegment(sketch, "E125.9.0.3", {"start": v(-2562.5, -4450) * mm, "end": v(-2562.5, -4420) * mm});
            skLineSegment(sketch, "E125.10.0.0", {"start": v(-2391.67, -4420) * mm, "end": v(-2361.67, -4420) * mm});
            skLineSegment(sketch, "E125.10.0.1", {"start": v(-2361.67, -4450) * mm, "end": v(-2361.67, -4420) * mm});
            skLineSegment(sketch, "E125.10.0.2", {"start": v(-2391.67, -4450) * mm, "end": v(-2361.67, -4450) * mm});
            skLineSegment(sketch, "E125.10.0.3", {"start": v(-2391.67, -4450) * mm, "end": v(-2391.67, -4420) * mm});
            skLineSegment(sketch, "E125.11.0.0", {"start": v(-2220.83, -4420) * mm, "end": v(-2190.83, -4420) * mm});
            skLineSegment(sketch, "E125.11.0.1", {"start": v(-2190.83, -4450) * mm, "end": v(-2190.83, -4420) * mm});
            skLineSegment(sketch, "E125.11.0.2", {"start": v(-2220.83, -4450) * mm, "end": v(-2190.83, -4450) * mm});
            skLineSegment(sketch, "E125.11.0.3", {"start": v(-2220.83, -4450) * mm, "end": v(-2220.83, -4420) * mm});
            skLineSegment(sketch, "E125.12.0.0", {"start": v(-2050, -4420) * mm, "end": v(-2020, -4420) * mm});
            skLineSegment(sketch, "E125.12.0.1", {"start": v(-2020, -4450) * mm, "end": v(-2020, -4420) * mm});
            skLineSegment(sketch, "E125.12.0.2", {"start": v(-2050, -4450) * mm, "end": v(-2020, -4450) * mm});
            skLineSegment(sketch, "E125.12.0.3", {"start": v(-2050, -4450) * mm, "end": v(-2050, -4420) * mm});
            skLineSegment(sketch, "E125.13.0.0", {"start": v(-1879.17, -4420) * mm, "end": v(-1849.17, -4420) * mm});
            skLineSegment(sketch, "E125.13.0.1", {"start": v(-1849.17, -4450) * mm, "end": v(-1849.17, -4420) * mm});
            skLineSegment(sketch, "E125.13.0.2", {"start": v(-1879.17, -4450) * mm, "end": v(-1849.17, -4450) * mm});
            skLineSegment(sketch, "E125.13.0.3", {"start": v(-1879.17, -4450) * mm, "end": v(-1879.17, -4420) * mm});
            skLineSegment(sketch, "E125.14.0.0", {"start": v(-1708.33, -4420) * mm, "end": v(-1678.33, -4420) * mm});
            skLineSegment(sketch, "E125.14.0.1", {"start": v(-1678.33, -4450) * mm, "end": v(-1678.33, -4420) * mm});
            skLineSegment(sketch, "E125.14.0.2", {"start": v(-1708.33, -4450) * mm, "end": v(-1678.33, -4450) * mm});
            skLineSegment(sketch, "E125.14.0.3", {"start": v(-1708.33, -4450) * mm, "end": v(-1708.33, -4420) * mm});
            skLineSegment(sketch, "E125.15.0.0", {"start": v(-1537.5, -4420) * mm, "end": v(-1507.5, -4420) * mm});
            skLineSegment(sketch, "E125.15.0.1", {"start": v(-1507.5, -4450) * mm, "end": v(-1507.5, -4420) * mm});
            skLineSegment(sketch, "E125.15.0.2", {"start": v(-1537.5, -4450) * mm, "end": v(-1507.5, -4450) * mm});
            skLineSegment(sketch, "E125.15.0.3", {"start": v(-1537.5, -4450) * mm, "end": v(-1537.5, -4420) * mm});
            skLineSegment(sketch, "E125.16.0.0", {"start": v(-1366.67, -4420) * mm, "end": v(-1336.67, -4420) * mm});
            skLineSegment(sketch, "E125.16.0.1", {"start": v(-1336.67, -4450) * mm, "end": v(-1336.67, -4420) * mm});
            skLineSegment(sketch, "E125.16.0.2", {"start": v(-1366.67, -4450) * mm, "end": v(-1336.67, -4450) * mm});
            skLineSegment(sketch, "E125.16.0.3", {"start": v(-1366.67, -4450) * mm, "end": v(-1366.67, -4420) * mm});
            skLineSegment(sketch, "E125.17.0.0", {"start": v(-1195.83, -4420) * mm, "end": v(-1165.83, -4420) * mm});
            skLineSegment(sketch, "E125.17.0.1", {"start": v(-1165.83, -4450) * mm, "end": v(-1165.83, -4420) * mm});
            skLineSegment(sketch, "E125.17.0.2", {"start": v(-1195.83, -4450) * mm, "end": v(-1165.83, -4450) * mm});
            skLineSegment(sketch, "E125.17.0.3", {"start": v(-1195.83, -4450) * mm, "end": v(-1195.83, -4420) * mm});
            skLineSegment(sketch, "E125.18.0.0", {"start": v(-1025, -4420) * mm, "end": v(-995, -4420) * mm});
            skLineSegment(sketch, "E125.18.0.1", {"start": v(-995, -4450) * mm, "end": v(-995, -4420) * mm});
            skLineSegment(sketch, "E125.18.0.2", {"start": v(-1025, -4450) * mm, "end": v(-995, -4450) * mm});
            skLineSegment(sketch, "E125.18.0.3", {"start": v(-1025, -4450) * mm, "end": v(-1025, -4420) * mm});
            skLineSegment(sketch, "E125.19.0.0", {"start": v(-854.17, -4420) * mm, "end": v(-824.17, -4420) * mm});
            skLineSegment(sketch, "E125.19.0.1", {"start": v(-824.17, -4450) * mm, "end": v(-824.17, -4420) * mm});
            skLineSegment(sketch, "E125.19.0.2", {"start": v(-854.17, -4450) * mm, "end": v(-824.17, -4450) * mm});
            skLineSegment(sketch, "E125.19.0.3", {"start": v(-854.17, -4450) * mm, "end": v(-854.17, -4420) * mm});
            skLineSegment(sketch, "E125.20.0.0", {"start": v(-683.33, -4420) * mm, "end": v(-653.33, -4420) * mm});
            skLineSegment(sketch, "E125.20.0.1", {"start": v(-653.33, -4450) * mm, "end": v(-653.33, -4420) * mm});
            skLineSegment(sketch, "E125.20.0.2", {"start": v(-683.33, -4450) * mm, "end": v(-653.33, -4450) * mm});
            skLineSegment(sketch, "E125.20.0.3", {"start": v(-683.33, -4450) * mm, "end": v(-683.33, -4420) * mm});
            skLineSegment(sketch, "E125.21.0.0", {"start": v(-512.5, -4420) * mm, "end": v(-482.5, -4420) * mm});
            skLineSegment(sketch, "E125.21.0.1", {"start": v(-482.5, -4450) * mm, "end": v(-482.5, -4420) * mm});
            skLineSegment(sketch, "E125.21.0.2", {"start": v(-512.5, -4450) * mm, "end": v(-482.5, -4450) * mm});
            skLineSegment(sketch, "E125.21.0.3", {"start": v(-512.5, -4450) * mm, "end": v(-512.5, -4420) * mm});
            skLineSegment(sketch, "E125.22.0.0", {"start": v(-341.67, -4420) * mm, "end": v(-311.67, -4420) * mm});
            skLineSegment(sketch, "E125.22.0.1", {"start": v(-311.67, -4450) * mm, "end": v(-311.67, -4420) * mm});
            skLineSegment(sketch, "E125.22.0.2", {"start": v(-341.67, -4450) * mm, "end": v(-311.67, -4450) * mm});
            skLineSegment(sketch, "E125.22.0.3", {"start": v(-341.67, -4450) * mm, "end": v(-341.67, -4420) * mm});
            skLineSegment(sketch, "E125.23.0.0", {"start": v(-170.83, -4420) * mm, "end": v(-140.83, -4420) * mm});
            skLineSegment(sketch, "E125.23.0.1", {"start": v(-140.83, -4450) * mm, "end": v(-140.83, -4420) * mm});
            skLineSegment(sketch, "E125.23.0.2", {"start": v(-170.83, -4450) * mm, "end": v(-140.83, -4450) * mm});
            skLineSegment(sketch, "E125.23.0.3", {"start": v(-170.83, -4450) * mm, "end": v(-170.83, -4420) * mm});
            skLineSegment(sketch, "E125.24.0.0", {"start": v(0, -4420) * mm, "end": v(30, -4420) * mm});
            skLineSegment(sketch, "E125.24.0.1", {"start": v(30, -4450) * mm, "end": v(30, -4420) * mm});
            skLineSegment(sketch, "E125.24.0.2", {"start": v(0, -4450) * mm, "end": v(30, -4450) * mm});
            skLineSegment(sketch, "E125.24.0.3", {"start": v(0, -4450) * mm, "end": v(0, -4420) * mm});
            skLineSegment(sketch, "E125.25.0.0", {"start": v(170.83, -4420) * mm, "end": v(200.83, -4420) * mm});
            skLineSegment(sketch, "E125.25.0.1", {"start": v(200.83, -4450) * mm, "end": v(200.83, -4420) * mm});
            skLineSegment(sketch, "E125.25.0.2", {"start": v(170.83, -4450) * mm, "end": v(200.83, -4450) * mm});
            skLineSegment(sketch, "E125.25.0.3", {"start": v(170.83, -4450) * mm, "end": v(170.83, -4420) * mm});
            skLineSegment(sketch, "E125.26.0.0", {"start": v(341.67, -4420) * mm, "end": v(371.67, -4420) * mm});
            skLineSegment(sketch, "E125.26.0.1", {"start": v(371.67, -4450) * mm, "end": v(371.67, -4420) * mm});
            skLineSegment(sketch, "E125.26.0.2", {"start": v(341.67, -4450) * mm, "end": v(371.67, -4450) * mm});
            skLineSegment(sketch, "E125.26.0.3", {"start": v(341.67, -4450) * mm, "end": v(341.67, -4420) * mm});
            skLineSegment(sketch, "E125.27.0.0", {"start": v(512.5, -4420) * mm, "end": v(542.5, -4420) * mm});
            skLineSegment(sketch, "E125.27.0.1", {"start": v(542.5, -4450) * mm, "end": v(542.5, -4420) * mm});
            skLineSegment(sketch, "E125.27.0.2", {"start": v(512.5, -4450) * mm, "end": v(542.5, -4450) * mm});
            skLineSegment(sketch, "E125.27.0.3", {"start": v(512.5, -4450) * mm, "end": v(512.5, -4420) * mm});
            skLineSegment(sketch, "E125.28.0.0", {"start": v(683.33, -4420) * mm, "end": v(713.33, -4420) * mm});
            skLineSegment(sketch, "E125.28.0.1", {"start": v(713.33, -4450) * mm, "end": v(713.33, -4420) * mm});
            skLineSegment(sketch, "E125.28.0.2", {"start": v(683.33, -4450) * mm, "end": v(713.33, -4450) * mm});
            skLineSegment(sketch, "E125.28.0.3", {"start": v(683.33, -4450) * mm, "end": v(683.33, -4420) * mm});
            skLineSegment(sketch, "E125.29.0.0", {"start": v(854.17, -4420) * mm, "end": v(884.17, -4420) * mm});
            skLineSegment(sketch, "E125.29.0.1", {"start": v(884.17, -4450) * mm, "end": v(884.17, -4420) * mm});
            skLineSegment(sketch, "E125.29.0.2", {"start": v(854.17, -4450) * mm, "end": v(884.17, -4450) * mm});
            skLineSegment(sketch, "E125.29.0.3", {"start": v(854.17, -4450) * mm, "end": v(854.17, -4420) * mm});
            skLineSegment(sketch, "E125.30.0.0", {"start": v(1025, -4420) * mm, "end": v(1055, -4420) * mm});
            skLineSegment(sketch, "E125.30.0.1", {"start": v(1055, -4450) * mm, "end": v(1055, -4420) * mm});
            skLineSegment(sketch, "E125.30.0.2", {"start": v(1025, -4450) * mm, "end": v(1055, -4450) * mm});
            skLineSegment(sketch, "E125.30.0.3", {"start": v(1025, -4450) * mm, "end": v(1025, -4420) * mm});
            skLineSegment(sketch, "E125.31.0.0", {"start": v(1195.83, -4420) * mm, "end": v(1225.83, -4420) * mm});
            skLineSegment(sketch, "E125.31.0.1", {"start": v(1225.83, -4450) * mm, "end": v(1225.83, -4420) * mm});
            skLineSegment(sketch, "E125.31.0.2", {"start": v(1195.83, -4450) * mm, "end": v(1225.83, -4450) * mm});
            skLineSegment(sketch, "E125.31.0.3", {"start": v(1195.83, -4450) * mm, "end": v(1195.83, -4420) * mm});
            skLineSegment(sketch, "E125.32.0.0", {"start": v(1366.67, -4420) * mm, "end": v(1396.67, -4420) * mm});
            skLineSegment(sketch, "E125.32.0.1", {"start": v(1396.67, -4450) * mm, "end": v(1396.67, -4420) * mm});
            skLineSegment(sketch, "E125.32.0.2", {"start": v(1366.67, -4450) * mm, "end": v(1396.67, -4450) * mm});
            skLineSegment(sketch, "E125.32.0.3", {"start": v(1366.67, -4450) * mm, "end": v(1366.67, -4420) * mm});
            skLineSegment(sketch, "E125.33.0.0", {"start": v(1537.5, -4420) * mm, "end": v(1567.5, -4420) * mm});
            skLineSegment(sketch, "E125.33.0.1", {"start": v(1567.5, -4450) * mm, "end": v(1567.5, -4420) * mm});
            skLineSegment(sketch, "E125.33.0.2", {"start": v(1537.5, -4450) * mm, "end": v(1567.5, -4450) * mm});
            skLineSegment(sketch, "E125.33.0.3", {"start": v(1537.5, -4450) * mm, "end": v(1537.5, -4420) * mm});
            skLineSegment(sketch, "E125.34.0.0", {"start": v(1708.33, -4420) * mm, "end": v(1738.33, -4420) * mm});
            skLineSegment(sketch, "E125.34.0.1", {"start": v(1738.33, -4450) * mm, "end": v(1738.33, -4420) * mm});
            skLineSegment(sketch, "E125.34.0.2", {"start": v(1708.33, -4450) * mm, "end": v(1738.33, -4450) * mm});
            skLineSegment(sketch, "E125.34.0.3", {"start": v(1708.33, -4450) * mm, "end": v(1708.33, -4420) * mm});
            skLineSegment(sketch, "E125.35.0.0", {"start": v(1879.17, -4420) * mm, "end": v(1909.17, -4420) * mm});
            skLineSegment(sketch, "E125.35.0.1", {"start": v(1909.17, -4450) * mm, "end": v(1909.17, -4420) * mm});
            skLineSegment(sketch, "E125.35.0.2", {"start": v(1879.17, -4450) * mm, "end": v(1909.17, -4450) * mm});
            skLineSegment(sketch, "E125.35.0.3", {"start": v(1879.17, -4450) * mm, "end": v(1879.17, -4420) * mm});
            skLineSegment(sketch, "E125.36.0.0", {"start": v(2050, -4420) * mm, "end": v(2080, -4420) * mm});
            skLineSegment(sketch, "E125.36.0.1", {"start": v(2080, -4450) * mm, "end": v(2080, -4420) * mm});
            skLineSegment(sketch, "E125.36.0.2", {"start": v(2050, -4450) * mm, "end": v(2080, -4450) * mm});
            skLineSegment(sketch, "E125.36.0.3", {"start": v(2050, -4450) * mm, "end": v(2050, -4420) * mm});
            skLineSegment(sketch, "E125.37.0.0", {"start": v(2220.83, -4420) * mm, "end": v(2250.83, -4420) * mm});
            skLineSegment(sketch, "E125.37.0.1", {"start": v(2250.83, -4450) * mm, "end": v(2250.83, -4420) * mm});
            skLineSegment(sketch, "E125.37.0.2", {"start": v(2220.83, -4450) * mm, "end": v(2250.83, -4450) * mm});
            skLineSegment(sketch, "E125.37.0.3", {"start": v(2220.83, -4450) * mm, "end": v(2220.83, -4420) * mm});
            skLineSegment(sketch, "E125.38.0.0", {"start": v(2391.67, -4420) * mm, "end": v(2421.67, -4420) * mm});
            skLineSegment(sketch, "E125.38.0.1", {"start": v(2421.67, -4450) * mm, "end": v(2421.67, -4420) * mm});
            skLineSegment(sketch, "E125.38.0.2", {"start": v(2391.67, -4450) * mm, "end": v(2421.67, -4450) * mm});
            skLineSegment(sketch, "E125.38.0.3", {"start": v(2391.67, -4450) * mm, "end": v(2391.67, -4420) * mm});
            skLineSegment(sketch, "E125.39.0.0", {"start": v(2562.5, -4420) * mm, "end": v(2592.5, -4420) * mm});
            skLineSegment(sketch, "E125.39.0.1", {"start": v(2592.5, -4450) * mm, "end": v(2592.5, -4420) * mm});
            skLineSegment(sketch, "E125.39.0.2", {"start": v(2562.5, -4450) * mm, "end": v(2592.5, -4450) * mm});
            skLineSegment(sketch, "E125.39.0.3", {"start": v(2562.5, -4450) * mm, "end": v(2562.5, -4420) * mm});
            skLineSegment(sketch, "E125.40.0.0", {"start": v(2733.33, -4420) * mm, "end": v(2763.33, -4420) * mm});
            skLineSegment(sketch, "E125.40.0.1", {"start": v(2763.33, -4450) * mm, "end": v(2763.33, -4420) * mm});
            skLineSegment(sketch, "E125.40.0.2", {"start": v(2733.33, -4450) * mm, "end": v(2763.33, -4450) * mm});
            skLineSegment(sketch, "E125.40.0.3", {"start": v(2733.33, -4450) * mm, "end": v(2733.33, -4420) * mm});
            skLineSegment(sketch, "E125.41.0.0", {"start": v(2904.17, -4420) * mm, "end": v(2934.17, -4420) * mm});
            skLineSegment(sketch, "E125.41.0.1", {"start": v(2934.17, -4450) * mm, "end": v(2934.17, -4420) * mm});
            skLineSegment(sketch, "E125.41.0.2", {"start": v(2904.17, -4450) * mm, "end": v(2934.17, -4450) * mm});
            skLineSegment(sketch, "E125.41.0.3", {"start": v(2904.17, -4450) * mm, "end": v(2904.17, -4420) * mm});
            skLineSegment(sketch, "E125.42.0.0", {"start": v(3075, -4420) * mm, "end": v(3105, -4420) * mm});
            skLineSegment(sketch, "E125.42.0.1", {"start": v(3105, -4450) * mm, "end": v(3105, -4420) * mm});
            skLineSegment(sketch, "E125.42.0.2", {"start": v(3075, -4450) * mm, "end": v(3105, -4450) * mm});
            skLineSegment(sketch, "E125.42.0.3", {"start": v(3075, -4450) * mm, "end": v(3075, -4420) * mm});
            skLineSegment(sketch, "E125.43.0.0", {"start": v(3245.83, -4420) * mm, "end": v(3275.83, -4420) * mm});
            skLineSegment(sketch, "E125.43.0.1", {"start": v(3275.83, -4450) * mm, "end": v(3275.83, -4420) * mm});
            skLineSegment(sketch, "E125.43.0.2", {"start": v(3245.83, -4450) * mm, "end": v(3275.83, -4450) * mm});
            skLineSegment(sketch, "E125.43.0.3", {"start": v(3245.83, -4450) * mm, "end": v(3245.83, -4420) * mm});
            skLineSegment(sketch, "E125.44.0.0", {"start": v(3416.67, -4420) * mm, "end": v(3446.67, -4420) * mm});
            skLineSegment(sketch, "E125.44.0.1", {"start": v(3446.67, -4450) * mm, "end": v(3446.67, -4420) * mm});
            skLineSegment(sketch, "E125.44.0.2", {"start": v(3416.67, -4450) * mm, "end": v(3446.67, -4450) * mm});
            skLineSegment(sketch, "E125.44.0.3", {"start": v(3416.67, -4450) * mm, "end": v(3416.67, -4420) * mm});
            skLineSegment(sketch, "E125.45.0.0", {"start": v(3587.5, -4420) * mm, "end": v(3617.5, -4420) * mm});
            skLineSegment(sketch, "E125.45.0.1", {"start": v(3617.5, -4450) * mm, "end": v(3617.5, -4420) * mm});
            skLineSegment(sketch, "E125.45.0.2", {"start": v(3587.5, -4450) * mm, "end": v(3617.5, -4450) * mm});
            skLineSegment(sketch, "E125.45.0.3", {"start": v(3587.5, -4450) * mm, "end": v(3587.5, -4420) * mm});
            skLineSegment(sketch, "E125.46.0.0", {"start": v(3758.33, -4420) * mm, "end": v(3788.33, -4420) * mm});
            skLineSegment(sketch, "E125.46.0.1", {"start": v(3788.33, -4450) * mm, "end": v(3788.33, -4420) * mm});
            skLineSegment(sketch, "E125.46.0.2", {"start": v(3758.33, -4450) * mm, "end": v(3788.33, -4450) * mm});
            skLineSegment(sketch, "E125.46.0.3", {"start": v(3758.33, -4450) * mm, "end": v(3758.33, -4420) * mm});
            skLineSegment(sketch, "E125.47.0.0", {"start": v(3929.17, -4420) * mm, "end": v(3959.17, -4420) * mm});
            skLineSegment(sketch, "E125.47.0.1", {"start": v(3959.17, -4450) * mm, "end": v(3959.17, -4420) * mm});
            skLineSegment(sketch, "E125.47.0.2", {"start": v(3929.17, -4450) * mm, "end": v(3959.17, -4450) * mm});
            skLineSegment(sketch, "E125.47.0.3", {"start": v(3929.17, -4450) * mm, "end": v(3929.17, -4420) * mm});
            skLineSegment(sketch, "E125.direction1", {"start": v(-4100, -4420) * mm, "end": v(-3929.17, -4420) * mm, "construction": true});
            skLineSegment(sketch, "E126.bottom", {"start": v(4100, -4450) * mm, "end": v(4070, -4450) * mm});
            skLineSegment(sketch, "E126.top", {"start": v(4100, -4420) * mm, "end": v(4070, -4420) * mm});
            skLineSegment(sketch, "E126.left", {"start": v(4100, -4450) * mm, "end": v(4100, -4420) * mm});
            skLineSegment(sketch, "E126.right", {"start": v(4070, -4450) * mm, "end": v(4070, -4420) * mm});
            skLineSegment(sketch, "E127.0.1.0", {"start": v(4100, -4220) * mm, "end": v(4070, -4220) * mm});
            skLineSegment(sketch, "E127.0.1.1", {"start": v(4070, -4250) * mm, "end": v(4070, -4220) * mm});
            skLineSegment(sketch, "E127.0.1.2", {"start": v(4100, -4250) * mm, "end": v(4070, -4250) * mm});
            skLineSegment(sketch, "E127.0.1.3", {"start": v(4100, -4250) * mm, "end": v(4100, -4220) * mm});
            skLineSegment(sketch, "E127.0.2.0", {"start": v(4100, -4020) * mm, "end": v(4070, -4020) * mm});
            skLineSegment(sketch, "E127.0.2.1", {"start": v(4070, -4050) * mm, "end": v(4070, -4020) * mm});
            skLineSegment(sketch, "E127.0.2.2", {"start": v(4100, -4050) * mm, "end": v(4070, -4050) * mm});
            skLineSegment(sketch, "E127.0.2.3", {"start": v(4100, -4050) * mm, "end": v(4100, -4020) * mm});
            skLineSegment(sketch, "E127.0.3.0", {"start": v(4100, -3820) * mm, "end": v(4070, -3820) * mm});
            skLineSegment(sketch, "E127.0.3.1", {"start": v(4070, -3850) * mm, "end": v(4070, -3820) * mm});
            skLineSegment(sketch, "E127.0.3.2", {"start": v(4100, -3850) * mm, "end": v(4070, -3850) * mm});
            skLineSegment(sketch, "E127.0.3.3", {"start": v(4100, -3850) * mm, "end": v(4100, -3820) * mm});
            skLineSegment(sketch, "E127.0.4.0", {"start": v(4100, -3620) * mm, "end": v(4070, -3620) * mm});
            skLineSegment(sketch, "E127.0.4.1", {"start": v(4070, -3650) * mm, "end": v(4070, -3620) * mm});
            skLineSegment(sketch, "E127.0.4.2", {"start": v(4100, -3650) * mm, "end": v(4070, -3650) * mm});
            skLineSegment(sketch, "E127.0.4.3", {"start": v(4100, -3650) * mm, "end": v(4100, -3620) * mm});
            skLineSegment(sketch, "E127.0.5.0", {"start": v(4100, -3420) * mm, "end": v(4070, -3420) * mm});
            skLineSegment(sketch, "E127.0.5.1", {"start": v(4070, -3450) * mm, "end": v(4070, -3420) * mm});
            skLineSegment(sketch, "E127.0.5.2", {"start": v(4100, -3450) * mm, "end": v(4070, -3450) * mm});
            skLineSegment(sketch, "E127.0.5.3", {"start": v(4100, -3450) * mm, "end": v(4100, -3420) * mm});
            skLineSegment(sketch, "E127.0.6.0", {"start": v(4100, -3220) * mm, "end": v(4070, -3220) * mm});
            skLineSegment(sketch, "E127.0.6.1", {"start": v(4070, -3250) * mm, "end": v(4070, -3220) * mm});
            skLineSegment(sketch, "E127.0.6.2", {"start": v(4100, -3250) * mm, "end": v(4070, -3250) * mm});
            skLineSegment(sketch, "E127.0.6.3", {"start": v(4100, -3250) * mm, "end": v(4100, -3220) * mm});
            skLineSegment(sketch, "E127.0.7.0", {"start": v(4100, -3020) * mm, "end": v(4070, -3020) * mm});
            skLineSegment(sketch, "E127.0.7.1", {"start": v(4070, -3050) * mm, "end": v(4070, -3020) * mm});
            skLineSegment(sketch, "E127.0.7.2", {"start": v(4100, -3050) * mm, "end": v(4070, -3050) * mm});
            skLineSegment(sketch, "E127.0.7.3", {"start": v(4100, -3050) * mm, "end": v(4100, -3020) * mm});
            skLineSegment(sketch, "E127.0.8.0", {"start": v(4100, -2820) * mm, "end": v(4070, -2820) * mm});
            skLineSegment(sketch, "E127.0.8.1", {"start": v(4070, -2850) * mm, "end": v(4070, -2820) * mm});
            skLineSegment(sketch, "E127.0.8.2", {"start": v(4100, -2850) * mm, "end": v(4070, -2850) * mm});
            skLineSegment(sketch, "E127.0.8.3", {"start": v(4100, -2850) * mm, "end": v(4100, -2820) * mm});
            skLineSegment(sketch, "E127.direction1", {"start": v(4070, -4420) * mm, "end": v(4095, -4420) * mm, "construction": true});
            skLineSegment(sketch, "E127.direction2", {"start": v(4070, -4420) * mm, "end": v(4070, -4220) * mm, "construction": true});
            skSolve(sketch);
        }
        {
            var Q0;
            Q0=makeQuery(id+"F16.imprint","IMPRINT",FACE,{"disambiguationData":[TD([[makeQuery(id+"F16.imprint","IMPRINT",EDGE,{"derivedFrom":sQuery(id+"F16.wireOp",EDGE,"E81")}),1.0]])]});
            var Q1;
            Q1=makeQuery(id+"F16.imprint","IMPRINT",FACE,{"disambiguationData":[TD([[makeQuery(id+"F16.imprint","IMPRINT",EDGE,{"derivedFrom":sQuery(id+"F16.wireOp",EDGE,"E87")}),1.0]])]});
            var Q2;
            Q2=makeQuery(id+"F16.imprint","IMPRINT",FACE,{"disambiguationData":[TD([[makeQuery(id+"F16.imprint","IMPRINT",EDGE,{"derivedFrom":sQuery(id+"F16.wireOp",EDGE,"E94")}),-1.0]])]});
            var Q3;
            Q3=makeQuery(id+"F16.imprint","IMPRINT",FACE,{"disambiguationData":[TD([[makeQuery(id+"F16.imprint","IMPRINT",EDGE,{"derivedFrom":sQuery(id+"F16.wireOp",EDGE,"E100")}),-1.0]])]});
            var Q4;
            Q4=makeQuery(id+"F16.imprint","IMPRINT",FACE,{"disambiguationData":[TD([[makeQuery(id+"F16.imprint","IMPRINT",EDGE,{"derivedFrom":sQuery(id+"F16.wireOp",EDGE,"E106")}),-1.0]])]});
            var Q5;
            {var subQ13=sQuery(id+"F16.wireOp",EDGE,"E75");Q5=makeQuery(id+"F16.imprint","IMPRINT",FACE,{"disambiguationData":[TD([[makeQuery(id+"F16.imprint","IMPRINT",EDGE,{"derivedFrom":subQ13}),1.0]])]});}
            var Q6;
            {var subQ0=sQuery(id+"F16.wireOp",EDGE,"E119");Q6=makeQuery(id+"F16.imprint","IMPRINT",FACE,{"disambiguationData":[TD([[makeQuery(id+"F16.imprint","IMPRINT",EDGE,{"derivedFrom":subQ0}),-1.0]])]});}
            var Q7;
            {var subQ0=sQuery(id+"F16.wireOp",EDGE,"E115");Q7=makeQuery(id+"F16.imprint","IMPRINT",FACE,{"disambiguationData":[TD([[makeQuery(id+"F16.imprint","IMPRINT",EDGE,{"derivedFrom":subQ0}),-1.0]])]});}
            extrude(context, id + "F17", {"entities" : qUnion([Q0, Q1, Q2, Q3, Q4, Q5, Q6, Q7]), "operationType" : NewBodyOperationType.ADD, "depth" : 2000 * mm, "offsetDistance" : 25 * mm});
        }
        {
            var Q0;
            Q0=qCreatedBy(id+"F2.planeOp",FACE);
            cPlane(context, id + "F18", {"entities" : qUnion([Q0]), "cplaneType" : CPlaneType.OFFSET, "offset" : 2200 * mm, "width" : 150 * mm, "height" : 150 * mm});
        }
        {
            var Q0;
            Q0=qCreatedBy(id+"F18.planeOp",FACE);
            var sketch = newSketch(context, id + "F19", { "sketchPlane" : qUnion([Q0])});
            skLineSegment(sketch, "E128.bottom", {"start": v(-4100, -4250) * mm, "end": v(4100, -4250) * mm});
            skLineSegment(sketch, "E128.top", {"start": v(100, 2750) * mm, "end": v(2600, 2750) * mm});
            skLineSegment(sketch, "E128.left", {"start": v(-4100, -4250) * mm, "end": v(-4100, 2750) * mm});
            skLineSegment(sketch, "E128.right", {"start": v(4100, -4250) * mm, "end": v(4100, -450) * mm});
            skLineSegment(sketch, "E129", {"start": v(4100, -450) * mm, "end": v(2600, -450) * mm});
            skLineSegment(sketch, "E130", {"start": v(2600, -450) * mm, "end": v(2600, 2750) * mm});
            skLineSegment(sketch, "E131", {"start": v(-3900, -4050) * mm, "end": v(3900, -4050) * mm});
            skLineSegment(sketch, "E132", {"start": v(3900, -4050) * mm, "end": v(3900, -750) * mm});
            skLineSegment(sketch, "E133", {"start": v(3900, -750) * mm, "end": v(2300, -750) * mm});
            skLineSegment(sketch, "E134", {"start": v(2300, -750) * mm, "end": v(2300, 2550) * mm});
            skLineSegment(sketch, "E135", {"start": v(100, 2750) * mm, "end": v(100, 4250) * mm});
            skLineSegment(sketch, "E136", {"start": v(100, 4250) * mm, "end": v(-4100, 4250) * mm});
            skLineSegment(sketch, "E137", {"start": v(-4100, 4250) * mm, "end": v(-4100, 2750) * mm});
            skLineSegment(sketch, "E138", {"start": v(-100, 2550) * mm, "end": v(-100, 4050) * mm});
            skLineSegment(sketch, "E139", {"start": v(-100, 4050) * mm, "end": v(-3900, 4050) * mm});
            skLineSegment(sketch, "E140", {"start": v(-3900, 4050) * mm, "end": v(-3900, -4050) * mm});
            skLineSegment(sketch, "E141", {"start": v(-100, 2550) * mm, "end": v(-3900, 2550) * mm});
            skLineSegment(sketch, "E142", {"start": v(-100, 2750) * mm, "end": v(-3900, 2750) * mm});
            skLineSegment(sketch, "E143.trimOffspring", {"start": v(2300, 2550) * mm, "end": v(-100, 2550) * mm});
            skLineSegment(sketch, "E144", {"start": v(2600, 2550) * mm, "end": v(4100, 2550) * mm});
            skLineSegment(sketch, "E145", {"start": v(4100, 2550) * mm, "end": v(4100, 3750) * mm});
            skLineSegment(sketch, "E146", {"start": v(4100, 3750) * mm, "end": v(2600, 3750) * mm});
            skLineSegment(sketch, "E147", {"start": v(2600, 3750) * mm, "end": v(2600, 2750) * mm});
            skLineSegment(sketch, "E148.bottom", {"start": v(2800, 2750) * mm, "end": v(3900, 2750) * mm});
            skLineSegment(sketch, "E148.top", {"start": v(2800, 3550) * mm, "end": v(3900, 3550) * mm});
            skLineSegment(sketch, "E148.left", {"start": v(2800, 2750) * mm, "end": v(2800, 3550) * mm});
            skLineSegment(sketch, "E148.right", {"start": v(3900, 2750) * mm, "end": v(3900, 3550) * mm});
            skLineSegment(sketch, "E149", {"start": v(2300, -750) * mm, "end": v(-3900, -750) * mm});
            skLineSegment(sketch, "E150", {"start": v(-3900, -500) * mm, "end": v(2300, -500) * mm});
            skLineSegment(sketch, "E151", {"start": v(-700, -4050) * mm, "end": v(-700, -750) * mm});
            skLineSegment(sketch, "E152", {"start": v(-800, -4050) * mm, "end": v(-800, -750) * mm});
            skLineSegment(sketch, "E153", {"start": v(2000, -4050) * mm, "end": v(2000, -750) * mm});
            skLineSegment(sketch, "E154", {"start": v(1900, -4050) * mm, "end": v(1900, -750) * mm});
            skLineSegment(sketch, "E155", {"start": v(-2800, -4050) * mm, "end": v(-2800, -2200) * mm});
            skLineSegment(sketch, "E156", {"start": v(-2800, -2200) * mm, "end": v(-3900, -2200) * mm});
            skLineSegment(sketch, "E157", {"start": v(-2900, -4050) * mm, "end": v(-2900, -2300) * mm});
            skLineSegment(sketch, "E158", {"start": v(-2900, -2300) * mm, "end": v(-3900, -2300) * mm});
            skLineSegment(sketch, "E159", {"start": v(-1800, -4050) * mm, "end": v(-1800, -2200) * mm});
            skLineSegment(sketch, "E160", {"start": v(-1800, -2200) * mm, "end": v(-800, -2200) * mm});
            skLineSegment(sketch, "E161", {"start": v(-1700, -4050) * mm, "end": v(-1700, -2300) * mm});
            skLineSegment(sketch, "E162", {"start": v(-1700, -2300) * mm, "end": v(-800, -2300) * mm});
            skSolve(sketch);
        }
        {
            var Q0;
            Q0=makeQuery(id+"F19.imprint","IMPRINT",FACE,{"disambiguationData":[TD([[makeQuery(id+"F19.imprint","IMPRINT",EDGE,{"derivedFrom":sQuery(id+"F19.wireOp",EDGE,"E128.bottom")}),1.0]])]});
            var Q1;
            {var subQ0=sQuery(id+"F19.wireOp",EDGE,"E141");Q1=makeQuery(id+"F19.imprint","IMPRINT",FACE,{"disambiguationData":[TD([[makeQuery(id+"F19.imprint","IMPRINT",EDGE,{"derivedFrom":subQ0}),-1.0]])]});}
            var Q2;
            {var subQ7=sQuery(id+"F19.wireOp",EDGE,"E150");Q2=makeQuery(id+"F19.imprint","IMPRINT",FACE,{"disambiguationData":[TD([[makeQuery(id+"F19.imprint","IMPRINT",EDGE,{"derivedFrom":subQ7}),-1.0]])]});}
            var Q3;
            {var subQ0=sQuery(id+"F19.wireOp",EDGE,"E153");Q3=makeQuery(id+"F19.imprint","IMPRINT",FACE,{"disambiguationData":[TD([[makeQuery(id+"F19.imprint","IMPRINT",EDGE,{"derivedFrom":subQ0}),1.0]])]});}
            var Q4;
            {var subQ0=sQuery(id+"F19.wireOp",EDGE,"E151");Q4=makeQuery(id+"F19.imprint","IMPRINT",FACE,{"disambiguationData":[TD([[makeQuery(id+"F19.imprint","IMPRINT",EDGE,{"derivedFrom":subQ0}),1.0]])]});}
            var Q5;
            {var subQ0=sQuery(id+"F19.wireOp",EDGE,"E155");Q5=makeQuery(id+"F19.imprint","IMPRINT",FACE,{"disambiguationData":[TD([[makeQuery(id+"F19.imprint","IMPRINT",EDGE,{"derivedFrom":subQ0}),1.0]])]});}
            var Q6;
            {var subQ0=sQuery(id+"F19.wireOp",EDGE,"E144");Q6=makeQuery(id+"F19.imprint","IMPRINT",FACE,{"disambiguationData":[TD([[makeQuery(id+"F19.imprint","IMPRINT",EDGE,{"derivedFrom":subQ0}),1.0]])]});}
            var Q7;
            {var subQ3=sQuery(id+"F19.wireOp",EDGE,"E159");Q7=makeQuery(id+"F19.imprint","IMPRINT",FACE,{"disambiguationData":[TD([[makeQuery(id+"F19.imprint","IMPRINT",EDGE,{"derivedFrom":subQ3}),-1.0]])]});}
            extrude(context, id + "F20", {"entities" : qUnion([Q0, Q1, Q2, Q3, Q4, Q5, Q6, Q7]), "oppositeDirection" : true, "depth" : 2200 * mm, "offsetDistance" : 25 * mm});
        }
        {
            var Q0;
            Q0=makeQuery(id+"F16.imprint","IMPRINT",FACE,{"disambiguationData":[TD([[makeQuery(id+"F16.imprint","IMPRINT",EDGE,{"derivedFrom":sQuery(id+"F16.wireOp",EDGE,"E122.bottom")}),-1.0]])]});
            var Q1;
            Q1=makeQuery(id+"F16.imprint","IMPRINT",FACE,{"disambiguationData":[TD([[makeQuery(id+"F16.imprint","IMPRINT",EDGE,{"derivedFrom":sQuery(id+"F16.wireOp",EDGE,"E123.0.1.0")}),1.0]])]});
            var Q2;
            Q2=makeQuery(id+"F16.imprint","IMPRINT",FACE,{"disambiguationData":[TD([[makeQuery(id+"F16.imprint","IMPRINT",EDGE,{"derivedFrom":sQuery(id+"F16.wireOp",EDGE,"E123.0.2.0")}),1.0]])]});
            var Q3;
            Q3=makeQuery(id+"F16.imprint","IMPRINT",FACE,{"disambiguationData":[TD([[makeQuery(id+"F16.imprint","IMPRINT",EDGE,{"derivedFrom":sQuery(id+"F16.wireOp",EDGE,"E123.0.3.0")}),1.0]])]});
            var Q4;
            Q4=makeQuery(id+"F16.imprint","IMPRINT",FACE,{"disambiguationData":[TD([[makeQuery(id+"F16.imprint","IMPRINT",EDGE,{"derivedFrom":sQuery(id+"F16.wireOp",EDGE,"E123.0.4.0")}),1.0]])]});
            var Q5;
            Q5=makeQuery(id+"F16.imprint","IMPRINT",FACE,{"disambiguationData":[TD([[makeQuery(id+"F16.imprint","IMPRINT",EDGE,{"derivedFrom":sQuery(id+"F16.wireOp",EDGE,"E123.0.5.0")}),1.0]])]});
            var Q6;
            Q6=makeQuery(id+"F16.imprint","IMPRINT",FACE,{"disambiguationData":[TD([[makeQuery(id+"F16.imprint","IMPRINT",EDGE,{"derivedFrom":sQuery(id+"F16.wireOp",EDGE,"E123.0.6.0")}),1.0]])]});
            var Q7;
            Q7=makeQuery(id+"F16.imprint","IMPRINT",FACE,{"disambiguationData":[TD([[makeQuery(id+"F16.imprint","IMPRINT",EDGE,{"derivedFrom":sQuery(id+"F16.wireOp",EDGE,"E123.0.7.0")}),1.0]])]});
            var Q8;
            Q8=makeQuery(id+"F16.imprint","IMPRINT",FACE,{"disambiguationData":[TD([[makeQuery(id+"F16.imprint","IMPRINT",EDGE,{"derivedFrom":sQuery(id+"F16.wireOp",EDGE,"E124.bottom")}),1.0]])]});
            var Q9;
            Q9=makeQuery(id+"F16.imprint","IMPRINT",FACE,{"disambiguationData":[TD([[makeQuery(id+"F16.imprint","IMPRINT",EDGE,{"derivedFrom":sQuery(id+"F16.wireOp",EDGE,"E125.1.0.0")}),-1.0]])]});
            var Q10;
            Q10=makeQuery(id+"F16.imprint","IMPRINT",FACE,{"disambiguationData":[TD([[makeQuery(id+"F16.imprint","IMPRINT",EDGE,{"derivedFrom":sQuery(id+"F16.wireOp",EDGE,"E125.2.0.0")}),-1.0]])]});
            var Q11;
            Q11=makeQuery(id+"F16.imprint","IMPRINT",FACE,{"disambiguationData":[TD([[makeQuery(id+"F16.imprint","IMPRINT",EDGE,{"derivedFrom":sQuery(id+"F16.wireOp",EDGE,"E125.3.0.0")}),-1.0]])]});
            var Q12;
            Q12=makeQuery(id+"F16.imprint","IMPRINT",FACE,{"disambiguationData":[TD([[makeQuery(id+"F16.imprint","IMPRINT",EDGE,{"derivedFrom":sQuery(id+"F16.wireOp",EDGE,"E125.4.0.0")}),-1.0]])]});
            var Q13;
            Q13=makeQuery(id+"F16.imprint","IMPRINT",FACE,{"disambiguationData":[TD([[makeQuery(id+"F16.imprint","IMPRINT",EDGE,{"derivedFrom":sQuery(id+"F16.wireOp",EDGE,"E125.5.0.0")}),-1.0]])]});
            var Q14;
            Q14=makeQuery(id+"F16.imprint","IMPRINT",FACE,{"disambiguationData":[TD([[makeQuery(id+"F16.imprint","IMPRINT",EDGE,{"derivedFrom":sQuery(id+"F16.wireOp",EDGE,"E125.6.0.0")}),-1.0]])]});
            var Q15;
            Q15=makeQuery(id+"F16.imprint","IMPRINT",FACE,{"disambiguationData":[TD([[makeQuery(id+"F16.imprint","IMPRINT",EDGE,{"derivedFrom":sQuery(id+"F16.wireOp",EDGE,"E125.7.0.0")}),-1.0]])]});
            var Q16;
            Q16=makeQuery(id+"F16.imprint","IMPRINT",FACE,{"disambiguationData":[TD([[makeQuery(id+"F16.imprint","IMPRINT",EDGE,{"derivedFrom":sQuery(id+"F16.wireOp",EDGE,"E125.8.0.0")}),-1.0]])]});
            var Q17;
            Q17=makeQuery(id+"F16.imprint","IMPRINT",FACE,{"disambiguationData":[TD([[makeQuery(id+"F16.imprint","IMPRINT",EDGE,{"derivedFrom":sQuery(id+"F16.wireOp",EDGE,"E125.9.0.0")}),-1.0]])]});
            var Q18;
            Q18=makeQuery(id+"F16.imprint","IMPRINT",FACE,{"disambiguationData":[TD([[makeQuery(id+"F16.imprint","IMPRINT",EDGE,{"derivedFrom":sQuery(id+"F16.wireOp",EDGE,"E125.10.0.0")}),-1.0]])]});
            var Q19;
            Q19=makeQuery(id+"F16.imprint","IMPRINT",FACE,{"disambiguationData":[TD([[makeQuery(id+"F16.imprint","IMPRINT",EDGE,{"derivedFrom":sQuery(id+"F16.wireOp",EDGE,"E125.11.0.0")}),-1.0]])]});
            var Q20;
            Q20=makeQuery(id+"F16.imprint","IMPRINT",FACE,{"disambiguationData":[TD([[makeQuery(id+"F16.imprint","IMPRINT",EDGE,{"derivedFrom":sQuery(id+"F16.wireOp",EDGE,"E125.12.0.0")}),-1.0]])]});
            var Q21;
            Q21=makeQuery(id+"F16.imprint","IMPRINT",FACE,{"disambiguationData":[TD([[makeQuery(id+"F16.imprint","IMPRINT",EDGE,{"derivedFrom":sQuery(id+"F16.wireOp",EDGE,"E125.13.0.0")}),-1.0]])]});
            var Q22;
            Q22=makeQuery(id+"F16.imprint","IMPRINT",FACE,{"disambiguationData":[TD([[makeQuery(id+"F16.imprint","IMPRINT",EDGE,{"derivedFrom":sQuery(id+"F16.wireOp",EDGE,"E125.14.0.0")}),-1.0]])]});
            var Q23;
            Q23=makeQuery(id+"F16.imprint","IMPRINT",FACE,{"disambiguationData":[TD([[makeQuery(id+"F16.imprint","IMPRINT",EDGE,{"derivedFrom":sQuery(id+"F16.wireOp",EDGE,"E125.15.0.0")}),-1.0]])]});
            var Q24;
            Q24=makeQuery(id+"F16.imprint","IMPRINT",FACE,{"disambiguationData":[TD([[makeQuery(id+"F16.imprint","IMPRINT",EDGE,{"derivedFrom":sQuery(id+"F16.wireOp",EDGE,"E125.16.0.0")}),-1.0]])]});
            var Q25;
            Q25=makeQuery(id+"F16.imprint","IMPRINT",FACE,{"disambiguationData":[TD([[makeQuery(id+"F16.imprint","IMPRINT",EDGE,{"derivedFrom":sQuery(id+"F16.wireOp",EDGE,"E125.17.0.0")}),-1.0]])]});
            var Q26;
            Q26=makeQuery(id+"F16.imprint","IMPRINT",FACE,{"disambiguationData":[TD([[makeQuery(id+"F16.imprint","IMPRINT",EDGE,{"derivedFrom":sQuery(id+"F16.wireOp",EDGE,"E125.18.0.0")}),-1.0]])]});
            var Q27;
            Q27=makeQuery(id+"F16.imprint","IMPRINT",FACE,{"disambiguationData":[TD([[makeQuery(id+"F16.imprint","IMPRINT",EDGE,{"derivedFrom":sQuery(id+"F16.wireOp",EDGE,"E125.19.0.0")}),-1.0]])]});
            var Q28;
            Q28=makeQuery(id+"F16.imprint","IMPRINT",FACE,{"disambiguationData":[TD([[makeQuery(id+"F16.imprint","IMPRINT",EDGE,{"derivedFrom":sQuery(id+"F16.wireOp",EDGE,"E125.20.0.0")}),-1.0]])]});
            var Q29;
            Q29=makeQuery(id+"F16.imprint","IMPRINT",FACE,{"disambiguationData":[TD([[makeQuery(id+"F16.imprint","IMPRINT",EDGE,{"derivedFrom":sQuery(id+"F16.wireOp",EDGE,"E125.21.0.0")}),-1.0]])]});
            var Q30;
            Q30=makeQuery(id+"F16.imprint","IMPRINT",FACE,{"disambiguationData":[TD([[makeQuery(id+"F16.imprint","IMPRINT",EDGE,{"derivedFrom":sQuery(id+"F16.wireOp",EDGE,"E125.22.0.0")}),-1.0]])]});
            var Q31;
            Q31=makeQuery(id+"F16.imprint","IMPRINT",FACE,{"disambiguationData":[TD([[makeQuery(id+"F16.imprint","IMPRINT",EDGE,{"derivedFrom":sQuery(id+"F16.wireOp",EDGE,"E125.23.0.0")}),-1.0]])]});
            var Q32;
            Q32=makeQuery(id+"F16.imprint","IMPRINT",FACE,{"disambiguationData":[TD([[makeQuery(id+"F16.imprint","IMPRINT",EDGE,{"derivedFrom":sQuery(id+"F16.wireOp",EDGE,"E125.26.0.0")}),-1.0]])]});
            var Q33;
            Q33=makeQuery(id+"F16.imprint","IMPRINT",FACE,{"disambiguationData":[TD([[makeQuery(id+"F16.imprint","IMPRINT",EDGE,{"derivedFrom":sQuery(id+"F16.wireOp",EDGE,"E125.27.0.0")}),-1.0]])]});
            var Q34;
            Q34=makeQuery(id+"F16.imprint","IMPRINT",FACE,{"disambiguationData":[TD([[makeQuery(id+"F16.imprint","IMPRINT",EDGE,{"derivedFrom":sQuery(id+"F16.wireOp",EDGE,"E125.29.0.0")}),-1.0]])]});
            var Q35;
            Q35=makeQuery(id+"F16.imprint","IMPRINT",FACE,{"disambiguationData":[TD([[makeQuery(id+"F16.imprint","IMPRINT",EDGE,{"derivedFrom":sQuery(id+"F16.wireOp",EDGE,"E125.28.0.0")}),-1.0]])]});
            var Q36;
            Q36=makeQuery(id+"F16.imprint","IMPRINT",FACE,{"disambiguationData":[TD([[makeQuery(id+"F16.imprint","IMPRINT",EDGE,{"derivedFrom":sQuery(id+"F16.wireOp",EDGE,"E125.25.0.0")}),-1.0]])]});
            var Q37;
            Q37=makeQuery(id+"F16.imprint","IMPRINT",FACE,{"disambiguationData":[TD([[makeQuery(id+"F16.imprint","IMPRINT",EDGE,{"derivedFrom":sQuery(id+"F16.wireOp",EDGE,"E125.24.0.0")}),-1.0]])]});
            var Q38;
            Q38=makeQuery(id+"F16.imprint","IMPRINT",FACE,{"disambiguationData":[TD([[makeQuery(id+"F16.imprint","IMPRINT",EDGE,{"derivedFrom":sQuery(id+"F16.wireOp",EDGE,"E125.44.0.0")}),-1.0]])]});
            var Q39;
            Q39=makeQuery(id+"F16.imprint","IMPRINT",FACE,{"disambiguationData":[TD([[makeQuery(id+"F16.imprint","IMPRINT",EDGE,{"derivedFrom":sQuery(id+"F16.wireOp",EDGE,"E125.47.0.0")}),-1.0]])]});
            var Q40;
            Q40=makeQuery(id+"F16.imprint","IMPRINT",FACE,{"disambiguationData":[TD([[makeQuery(id+"F16.imprint","IMPRINT",EDGE,{"derivedFrom":sQuery(id+"F16.wireOp",EDGE,"E125.34.0.0")}),-1.0]])]});
            var Q41;
            Q41=makeQuery(id+"F16.imprint","IMPRINT",FACE,{"disambiguationData":[TD([[makeQuery(id+"F16.imprint","IMPRINT",EDGE,{"derivedFrom":sQuery(id+"F16.wireOp",EDGE,"E125.31.0.0")}),-1.0]])]});
            var Q42;
            Q42=makeQuery(id+"F16.imprint","IMPRINT",FACE,{"disambiguationData":[TD([[makeQuery(id+"F16.imprint","IMPRINT",EDGE,{"derivedFrom":sQuery(id+"F16.wireOp",EDGE,"E125.37.0.0")}),-1.0]])]});
            var Q43;
            Q43=makeQuery(id+"F16.imprint","IMPRINT",FACE,{"disambiguationData":[TD([[makeQuery(id+"F16.imprint","IMPRINT",EDGE,{"derivedFrom":sQuery(id+"F16.wireOp",EDGE,"E125.36.0.0")}),-1.0]])]});
            var Q44;
            Q44=makeQuery(id+"F16.imprint","IMPRINT",FACE,{"disambiguationData":[TD([[makeQuery(id+"F16.imprint","IMPRINT",EDGE,{"derivedFrom":sQuery(id+"F16.wireOp",EDGE,"E125.38.0.0")}),-1.0]])]});
            var Q45;
            Q45=makeQuery(id+"F16.imprint","IMPRINT",FACE,{"disambiguationData":[TD([[makeQuery(id+"F16.imprint","IMPRINT",EDGE,{"derivedFrom":sQuery(id+"F16.wireOp",EDGE,"E125.45.0.0")}),-1.0]])]});
            var Q46;
            Q46=makeQuery(id+"F16.imprint","IMPRINT",FACE,{"disambiguationData":[TD([[makeQuery(id+"F16.imprint","IMPRINT",EDGE,{"derivedFrom":sQuery(id+"F16.wireOp",EDGE,"E125.40.0.0")}),-1.0]])]});
            var Q47;
            Q47=makeQuery(id+"F16.imprint","IMPRINT",FACE,{"disambiguationData":[TD([[makeQuery(id+"F16.imprint","IMPRINT",EDGE,{"derivedFrom":sQuery(id+"F16.wireOp",EDGE,"E125.43.0.0")}),-1.0]])]});
            var Q48;
            Q48=makeQuery(id+"F16.imprint","IMPRINT",FACE,{"disambiguationData":[TD([[makeQuery(id+"F16.imprint","IMPRINT",EDGE,{"derivedFrom":sQuery(id+"F16.wireOp",EDGE,"E125.42.0.0")}),-1.0]])]});
            var Q49;
            Q49=makeQuery(id+"F16.imprint","IMPRINT",FACE,{"disambiguationData":[TD([[makeQuery(id+"F16.imprint","IMPRINT",EDGE,{"derivedFrom":sQuery(id+"F16.wireOp",EDGE,"E125.46.0.0")}),-1.0]])]});
            var Q50;
            Q50=makeQuery(id+"F16.imprint","IMPRINT",FACE,{"disambiguationData":[TD([[makeQuery(id+"F16.imprint","IMPRINT",EDGE,{"derivedFrom":sQuery(id+"F16.wireOp",EDGE,"E125.35.0.0")}),-1.0]])]});
            var Q51;
            Q51=makeQuery(id+"F16.imprint","IMPRINT",FACE,{"disambiguationData":[TD([[makeQuery(id+"F16.imprint","IMPRINT",EDGE,{"derivedFrom":sQuery(id+"F16.wireOp",EDGE,"E125.33.0.0")}),-1.0]])]});
            var Q52;
            Q52=makeQuery(id+"F16.imprint","IMPRINT",FACE,{"disambiguationData":[TD([[makeQuery(id+"F16.imprint","IMPRINT",EDGE,{"derivedFrom":sQuery(id+"F16.wireOp",EDGE,"E125.30.0.0")}),-1.0]])]});
            var Q53;
            Q53=makeQuery(id+"F16.imprint","IMPRINT",FACE,{"disambiguationData":[TD([[makeQuery(id+"F16.imprint","IMPRINT",EDGE,{"derivedFrom":sQuery(id+"F16.wireOp",EDGE,"E125.41.0.0")}),-1.0]])]});
            var Q54;
            Q54=makeQuery(id+"F16.imprint","IMPRINT",FACE,{"disambiguationData":[TD([[makeQuery(id+"F16.imprint","IMPRINT",EDGE,{"derivedFrom":sQuery(id+"F16.wireOp",EDGE,"E125.39.0.0")}),-1.0]])]});
            var Q55;
            Q55=makeQuery(id+"F16.imprint","IMPRINT",FACE,{"disambiguationData":[TD([[makeQuery(id+"F16.imprint","IMPRINT",EDGE,{"derivedFrom":sQuery(id+"F16.wireOp",EDGE,"E125.32.0.0")}),-1.0]])]});
            var Q56;
            Q56=makeQuery(id+"F16.imprint","IMPRINT",FACE,{"disambiguationData":[TD([[makeQuery(id+"F16.imprint","IMPRINT",EDGE,{"derivedFrom":sQuery(id+"F16.wireOp",EDGE,"E126.bottom")}),1.0]])]});
            var Q57;
            Q57=makeQuery(id+"F16.imprint","IMPRINT",FACE,{"disambiguationData":[TD([[makeQuery(id+"F16.imprint","IMPRINT",EDGE,{"derivedFrom":sQuery(id+"F16.wireOp",EDGE,"E127.0.2.0")}),1.0]])]});
            var Q58;
            Q58=makeQuery(id+"F16.imprint","IMPRINT",FACE,{"disambiguationData":[TD([[makeQuery(id+"F16.imprint","IMPRINT",EDGE,{"derivedFrom":sQuery(id+"F16.wireOp",EDGE,"E127.0.3.0")}),1.0]])]});
            var Q59;
            Q59=makeQuery(id+"F16.imprint","IMPRINT",FACE,{"disambiguationData":[TD([[makeQuery(id+"F16.imprint","IMPRINT",EDGE,{"derivedFrom":sQuery(id+"F16.wireOp",EDGE,"E127.0.1.0")}),1.0]])]});
            var Q60;
            Q60=makeQuery(id+"F16.imprint","IMPRINT",FACE,{"disambiguationData":[TD([[makeQuery(id+"F16.imprint","IMPRINT",EDGE,{"derivedFrom":sQuery(id+"F16.wireOp",EDGE,"E127.0.5.0")}),1.0]])]});
            var Q61;
            Q61=makeQuery(id+"F16.imprint","IMPRINT",FACE,{"disambiguationData":[TD([[makeQuery(id+"F16.imprint","IMPRINT",EDGE,{"derivedFrom":sQuery(id+"F16.wireOp",EDGE,"E127.0.8.0")}),1.0]])]});
            var Q62;
            Q62=makeQuery(id+"F16.imprint","IMPRINT",FACE,{"disambiguationData":[TD([[makeQuery(id+"F16.imprint","IMPRINT",EDGE,{"derivedFrom":sQuery(id+"F16.wireOp",EDGE,"E127.0.6.0")}),1.0]])]});
            var Q63;
            Q63=makeQuery(id+"F16.imprint","IMPRINT",FACE,{"disambiguationData":[TD([[makeQuery(id+"F16.imprint","IMPRINT",EDGE,{"derivedFrom":sQuery(id+"F16.wireOp",EDGE,"E127.0.4.0")}),1.0]])]});
            var Q64;
            Q64=makeQuery(id+"F16.imprint","IMPRINT",FACE,{"disambiguationData":[TD([[makeQuery(id+"F16.imprint","IMPRINT",EDGE,{"derivedFrom":sQuery(id+"F16.wireOp",EDGE,"E127.0.7.0")}),1.0]])]});
            var Q65;
            {var subQ0=sQuery(id+"F16.wireOp",EDGE,"E109");Q65=makeQuery(id+"F16.imprint","IMPRINT",FACE,{"disambiguationData":[TD([[makeQuery(id+"F16.imprint","IMPRINT",EDGE,{"derivedFrom":subQ0}),1.0]])]});}
            extrude(context, id + "F21", {"entities" : qUnion([Q0, Q1, Q2, Q3, Q4, Q5, Q6, Q7, Q8, Q9, Q10, Q11, Q12, Q13, Q14, Q15, Q16, Q17, Q18, Q19, Q20, Q21, Q22, Q23, Q24, Q25, Q26, Q27, Q28, Q29, Q30, Q31, Q32, Q33, Q34, Q35, Q36, Q37, Q38, Q39, Q40, Q41, Q42, Q43, Q44, Q45, Q46, Q47, Q48, Q49, Q50, Q51, Q52, Q53, Q54, Q55, Q56, Q57, Q58, Q59, Q60, Q61, Q62, Q63, Q64, Q65]), "operationType" : NewBodyOperationType.ADD, "depth" : 1000 * mm, "offsetDistance" : 25 * mm, "hasSecondDirection" : true, "secondDirectionOppositeDirection" : true, "secondDirectionDepth" : 25 * mm});
        }
        {
            var Q0;
            Q0=qCreatedBy(makeId("Top.planeOp"),FACE);
            cPlane(context, id + "F22", {"entities" : qUnion([Q0]), "cplaneType" : CPlaneType.OFFSET, "offset" : 1300 * mm, "oppositeDirection" : true, "width" : 150 * mm, "height" : 150 * mm});
        }
        {
            var Q0;
            Q0=qCreatedBy(id+"F22.planeOp",FACE);
            var sketch = newSketch(context, id + "F23", { "sketchPlane" : qUnion([Q0])});
            skLineSegment(sketch, "E163.bottom", {"start": v(-10500, 4250) * mm, "end": v(10500, 4250) * mm});
            skLineSegment(sketch, "E163.top", {"start": v(-10500, -22750) * mm, "end": v(10500, -22750) * mm});
            skLineSegment(sketch, "E163.left", {"start": v(-10500, 4250) * mm, "end": v(-10500, -22750) * mm});
            skLineSegment(sketch, "E163.right", {"start": v(10500, 4250) * mm, "end": v(10500, -22750) * mm});
            skLineSegment(sketch, "E164", {"start": v(-4100, 4250) * mm, "end": v(-4100, -4250) * mm});
            skLineSegment(sketch, "E165", {"start": v(-4100, -4250) * mm, "end": v(4100, -4250) * mm});
            skLineSegment(sketch, "E166", {"start": v(4100, -4250) * mm, "end": v(4100, 4250) * mm});
            skSolve(sketch);
        }
        {
            var Q0;
            Q0=makeQuery(id+"F23.imprint","IMPRINT",FACE,{"disambiguationData":[TD([[makeQuery(id+"F23.imprint","IMPRINT",EDGE,{"derivedFrom":sQuery(id+"F23.wireOp",EDGE,"E163.top")}),1.0]])]});
            extrude(context, id + "F24", {"entities" : qUnion([Q0]), "depth" : 100 * mm, "offsetDistance" : 25 * mm});
        }
        {
            var Q0;
            Q0=makeQuery(id+"F21.opExtrude","CAP_FACE",FACE,{"disambiguationData":[OSD([sQuery(id+"F16.wireOp",EDGE,"E122.bottom"),sQuery(id+"F16.wireOp",EDGE,"E122.top"),sQuery(id+"F16.wireOp",EDGE,"E122.left"),sQuery(id+"F16.wireOp",EDGE,"E122.right")])],"isStart":false});
            var sketch = newSketch(context, id + "F25", { "sketchPlane" : qUnion([Q0])});
            skLineSegment(sketch, "E167", {"start": v(-4100, -2880) * mm, "end": v(-4100, -4450) * mm});
            skLineSegment(sketch, "E168", {"start": v(-4100, -4450) * mm, "end": v(4100, -4450) * mm});
            skLineSegment(sketch, "E169", {"start": v(4100, -4450) * mm, "end": v(4100, -2780) * mm});
            skLineSegment(sketch, "E170", {"start": v(4100, -2780) * mm, "end": v(4070, -2780) * mm});
            skLineSegment(sketch, "E171", {"start": v(4070, -2780) * mm, "end": v(4070, -4420) * mm});
            skLineSegment(sketch, "E172", {"start": v(4070, -4420) * mm, "end": v(-4070, -4420) * mm});
            skLineSegment(sketch, "E173", {"start": v(-4070, -4420) * mm, "end": v(-4070, -2780) * mm});
            skLineSegment(sketch, "E174", {"start": v(-4070, -2780) * mm, "end": v(-4100, -2780) * mm});
            skLineSegment(sketch, "E175", {"start": v(-4100, -2780) * mm, "end": v(-4100, -2880) * mm});
            skSolve(sketch);
        }
        {
            var Q0;
            {var subQ0=sQuery(id+"F25.wireOp",EDGE,"E168");Q0=makeQuery(id+"F25.imprint","IMPRINT",FACE,{"disambiguationData":[TD([[makeQuery(id+"F25.imprint","IMPRINT",EDGE,{"derivedFrom":subQ0}),1.0]])]});}
            var Q1;
            {var subQ1=makeQuery(id+"F21.opExtrude","CAP_EDGE",EDGE,{"disambiguationData":[OSD([sQuery(id+"F16.wireOp",EDGE,"E122.bottom")])],"isStart":false});Q1=makeQuery(id+"F25.imprint","IMPRINT",FACE,{"disambiguationData":[TD([[makeQuery(id+"F25.imprint","IMPRINT",EDGE,{"derivedFrom":subQ1}),-1.0]])]});}
            var Q2;
            {var subQ2=sQuery(id+"F25.wireOp",EDGE,"E174");Q2=makeQuery(id+"F25.imprint","IMPRINT",FACE,{"disambiguationData":[TD([[makeQuery(id+"F25.imprint","IMPRINT",EDGE,{"derivedFrom":subQ2}),1.0]])]});}
            extrude(context, id + "F26", {"entities" : qUnion([Q0, Q1, Q2]), "operationType" : NewBodyOperationType.ADD, "depth" : 50 * mm, "offsetDistance" : 25 * mm});
        }
    });
